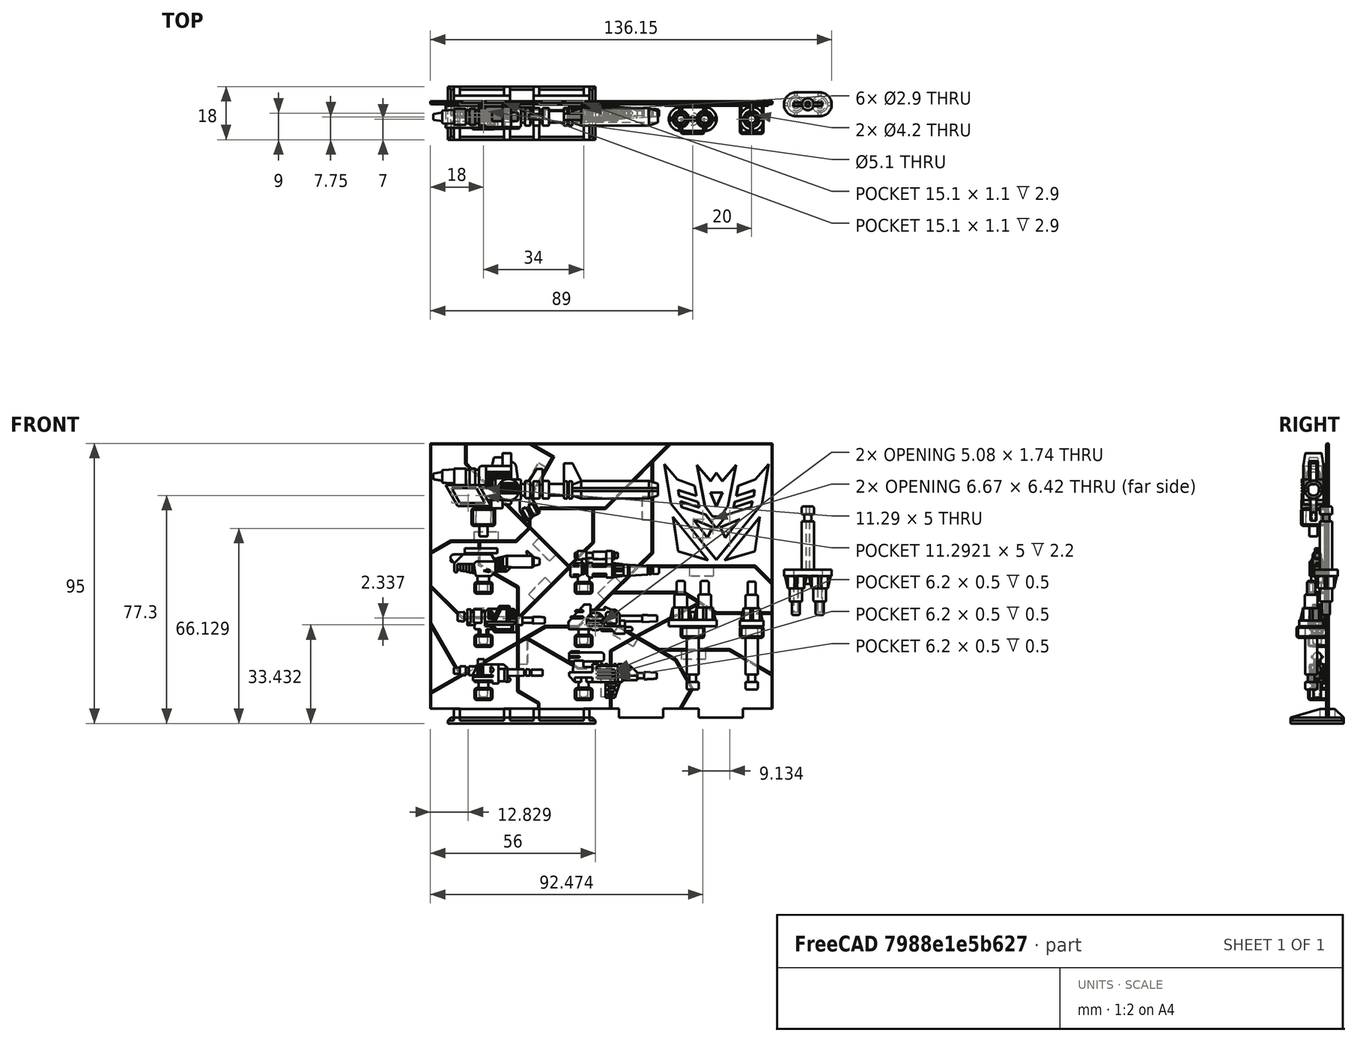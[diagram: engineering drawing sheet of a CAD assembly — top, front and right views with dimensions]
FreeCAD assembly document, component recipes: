
FREECAD ASSEMBLY — COMPONENT RECIPES ("Accesories")

This assembly document has 10 components, labeled P0..P9 below (a component is one placed body or linked part). 9 of them carry a construction recipe — the FreeCAD feature program that regenerates the part from scratch, quoted from this document or its linked companion documents; the rest are supplied as boundary geometry only. No exploded tour is included for this assembly.
NOTE — this tour is split across 3 documents so each fits a 32k-token context. This is document 1: the component sections continue in the remaining 2 documents, each repeating the header above.
COMPONENT P0 — recipe-attached ("Bonecrusher_Gun", modeled in this document).
Construction recipe (the document's own serialized feature program — sketch geometry with constraints, then the solid features built on it; lengths are millimeters unless a unit is written):

FEATURE [Sketcher::SketchObject] Sketch
  ArcFitTolerance = 1e-06
  AttachmentSupport = -> [YZ_Plane]
  FullyConstrained = true
  MakeInternals = false
  MapMode = 5
  Placement = pos=(0,0,0) rot=(0.57735,0.57735,0.57735;2.0944rad)
  sketch-geometry (1):
    g0: Circle CenterX=0 CenterY=0 CenterZ=0 NormalX=0 NormalY=0 NormalZ=1 AngleXU=0 Radius=2.25
  constraints (2):
    c: Coincident(g0,g-1)
    c: Diameter(g0) = 4.5
FEATURE [PartDesign::Pad] Pad
  Direction = (1,0,0)
  Length = 4.9
  Length2 = 10
  Placement = pos=(0,0,0) rot=(1,1,1;2.0944rad)
  Profile = -> Sketch
  ReferenceAxis = -> Sketch [N_Axis]
  Refine = true
  Suppressed = false
  Type = 0
FEATURE [Sketcher::SketchObject] Sketch001
  ArcFitTolerance = 1e-06
  AttachmentSupport = -> [Pad]
  FullyConstrained = true
  MakeInternals = false
  MapMode = 5
  Placement = pos=(4.9,0,0) rot=(0.57735,0.57735,0.57735;2.0944rad)
  sketch-geometry (1):
    g0: Circle CenterX=0 CenterY=0 CenterZ=0 NormalX=0 NormalY=0 NormalZ=1 AngleXU=0 Radius=2.45
  constraints (2):
    c: Coincident(g0,g-1)
    c: Diameter(g0) = 4.9
FEATURE [PartDesign::AdditiveLoft] AdditiveLoft
  BaseFeature = -> Pad
  Closed = false
  Placement = pos=(0,0,0) rot=(1,1,1;2.0944rad)
  Profile = -> Sketch001
  Refine = true
  Ruled = false
  Sections = -> [Pad]
  Suppressed = false
FEATURE [PartDesign::Fillet] Fillet
  Base = -> AdditiveLoft [Edge1]
  BaseFeature = -> AdditiveLoft
  Placement = pos=(0,0,0) rot=(1,1,1;2.0944rad)
  Radius = 0.5
  Refine = true
  SupportTransform = false
  Suppressed = false
  UseAllEdges = false
FEATURE [Sketcher::SketchObject] Sketch002
  ArcFitTolerance = 1e-06
  AttachmentSupport = -> [XZ_Plane]
  FullyConstrained = true
  MakeInternals = false
  MapMode = 5
  Placement = pos=(0,0,0) rot=(1,0,0;1.5708rad)
  sketch-geometry (4):
    g0: LineSegment StartX=4.2 StartY=2.5 StartZ=0 EndX=4 EndY=2.5 EndZ=0
    g1: LineSegment StartX=4 StartY=2.5 StartZ=0 EndX=4 EndY=2.3 EndZ=0
    g2: LineSegment StartX=4 StartY=2.3 StartZ=0 EndX=4.2 EndY=2.3 EndZ=0
    g3: LineSegment StartX=4.2 StartY=2.3 StartZ=0 EndX=4.2 EndY=2.5 EndZ=0
  constraints (12):
    c: Coincident(g0,g1)
    c: Coincident(g1,g2)
    c: Coincident(g2,g3)
    c: Coincident(g3,g0)
    c: Horizontal(g0)
    c: Horizontal(g2)
    c: Vertical(g1)
    c: Vertical(g3)
    c: DistanceX(g-1,g1) = 4
    c: DistanceX(g0,g0) = 0.2
    c: DistanceY(g3,g3) = 0.2
    c: DistanceY(g-1,g1) = 2.3
FEATURE [PartDesign::Groove] Groove
  Angle = 360
  Angle2 = 60
  Axis = (1,0,0)
  Base = (0,0,0)
  BaseFeature = -> Fillet
  Placement = pos=(0,0,0) rot=(1,1,1;2.0944rad)
  Profile = -> Sketch002
  ReferenceAxis = -> Sketch002 [H_Axis]
  Refine = true
  Reversed = true
  Suppressed = false
  Type = 0
FEATURE [Sketcher::SketchObject] Sketch003
  ArcFitTolerance = 1e-06
  AttachmentOffset = pos=(0,0,-1) rot=(0,0,1;0rad)
  AttachmentSupport = -> [Groove]
  FullyConstrained = true
  MakeInternals = false
  MapMode = 5
  Placement = pos=(1,0,0) rot=(0.57735,0.57735,-0.57735;4.18879rad)
  sketch-geometry (20):
    g0: LineSegment StartX=-1.5 StartY=1.5 StartZ=0 EndX=-1.32322 EndY=1.67678 EndZ=0
    g1: LineSegment StartX=-1.32322 StartY=1.67678 StartZ=0 EndX=-1.67678 EndY=2.03033 EndZ=0
    g2: LineSegment StartX=-1.67678 StartY=2.03033 StartZ=0 EndX=-2.03033 EndY=1.67678 EndZ=0
    g3: LineSegment StartX=-1.5 StartY=1.5 StartZ=0 EndX=-1.67678 EndY=1.32322 EndZ=0
    g4: LineSegment StartX=-1.67678 StartY=1.32322 StartZ=0 EndX=-2.03033 EndY=1.67678 EndZ=0
    g5: LineSegment StartX=-1.5 StartY=-1.5 StartZ=0 EndX=-1.67678 EndY=-1.32322 EndZ=0
    g6: LineSegment StartX=-1.67678 StartY=-1.32322 StartZ=0 EndX=-2.03033 EndY=-1.67678 EndZ=0
    g7: LineSegment StartX=-2.03033 StartY=-1.67678 StartZ=0 EndX=-1.67678 EndY=-2.03033 EndZ=0
    g8: LineSegment StartX=-1.67678 StartY=-2.03033 StartZ=0 EndX=-1.32322 EndY=-1.67678 EndZ=0
    g9: LineSegment StartX=-1.32322 StartY=-1.67678 StartZ=0 EndX=-1.5 EndY=-1.5 EndZ=0
    g10: LineSegment StartX=1.5 StartY=-1.5 StartZ=0 EndX=1.32322 EndY=-1.67678 EndZ=0
    g11: LineSegment StartX=1.32322 StartY=-1.67678 StartZ=0 EndX=1.67678 EndY=-2.03033 EndZ=0
    g12: LineSegment StartX=1.67678 StartY=-2.03033 StartZ=0 EndX=2.03033 EndY=-1.67678 EndZ=0
    g13: LineSegment StartX=2.03033 StartY=-1.67678 StartZ=0 EndX=1.67678 EndY=-1.32322 EndZ=0
    g14: LineSegment StartX=1.67678 StartY=-1.32322 StartZ=0 EndX=1.5 EndY=-1.5 EndZ=0
    g15: LineSegment StartX=1.5 StartY=1.5 StartZ=0 EndX=1.67678 EndY=1.32322 EndZ=0
    g16: LineSegment StartX=1.67678 StartY=1.32322 StartZ=0 EndX=2.03033 EndY=1.67678 EndZ=0
    g17: LineSegment StartX=2.03033 StartY=1.67678 StartZ=0 EndX=1.67678 EndY=2.03033 EndZ=0
    g18: LineSegment StartX=1.67678 StartY=2.03033 StartZ=0 EndX=1.32322 EndY=1.67678 EndZ=0
    g19: LineSegment StartX=1.32322 StartY=1.67678 StartZ=0 EndX=1.5 EndY=1.5 EndZ=0
  constraints (60):
    c: Coincident(g1,g0)
    c: Coincident(g2,g1)
    c: Coincident(g3,g0)
    c: Coincident(g4,g3)
    c: Coincident(g4,g2)
    c: Angle(g-1,g3) = 0.785398
    c: Angle(g0) = 0.785398
    c: Distance(g0) = 0.25
    c: Distance(g3) = 0.25
    c: Distance(g2) = 0.5
    c: Distance(g4) = 0.5
    c: Distance(g1) = 0.5
    c: Angle(g2,g1) = 1.5708
    c: DistanceY(g-1,g0) = 1.5
    c: DistanceX(g0,g-1) = 1.5
    c: Coincident(g6,g5)
    c: Coincident(g7,g6)
    c: Coincident(g8,g7)
    c: Coincident(g9,g8)
    c: Coincident(g9,g5)
    c: Coincident(g11,g10)
    c: Coincident(g12,g11)
    c: Coincident(g13,g12)
    c: Coincident(g14,g13)
    c: Coincident(g14,g10)
    c: Coincident(g16,g15)
    c: Coincident(g17,g16)
    c: Coincident(g18,g17)
    c: Coincident(g19,g18)
    c: Coincident(g19,g15)
    c: DistanceY(g-1,g15) = 1.5
    c: DistanceY(g10,g-1) = 1.5
    c: DistanceY(g5,g-1) = 1.5
    c: DistanceX(g5,g-1) = 1.5
    c: DistanceX(g-1,g15) = 1.5
    c: DistanceX(g-1,g10) = 1.5
    c: Distance(g18) = 0.5
    c: Distance(g17) = 0.5
    c: Distance(g16) = 0.5
    c: Distance(g19) = 0.25
    c: Distance(g15) = 0.25
    c: Distance(g14) = 0.25
    c: Distance(g10) = 0.25
    c: Distance(g9) = 0.25
    c: Distance(g5) = 0.25
    c: Distance(g6) = 0.5
    c: Distance(g7) = 0.5
    c: Distance(g8) = 0.5
    c: Distance(g11) = 0.5
    c: Distance(g12) = 0.5
    c: Distance(g13) = 0.5
    c: Angle(g12,g11) = 1.5708
    c: Angle(g8,g7) = 1.5708
    c: Angle(g17,g16) = 1.5708
    c: Angle(g15,g19) = 3.14159
    c: Angle(g14,g10) = 3.14159
    c: Angle(g5,g9) = 3.14159
    c: Angle(g9,g-1) = 0.785398
    c: Angle(g-1,g10) = 0.785398
    c: Angle(g-2,g19) = 0.785398
FEATURE [PartDesign::Pocket] Pocket
  BaseFeature = -> Groove
  Direction = (1,0,0)
  Length = 2
  Length2 = 5
  Placement = pos=(0,0,0) rot=(1,1,1;2.0944rad)
  Profile = -> Sketch003
  ReferenceAxis = -> Sketch003 [N_Axis]
  Refine = true
  Suppressed = false
  Type = 0
FEATURE [Sketcher::SketchObject] Sketch004
  ArcFitTolerance = 1e-06
  AttachmentSupport = -> [Pocket]
  FullyConstrained = true
  MakeInternals = false
  MapMode = 5
  Placement = pos=(4.9,0,0) rot=(0.57735,0.57735,0.57735;2.0944rad)
  sketch-geometry (1):
    g0: Circle CenterX=0 CenterY=0 CenterZ=0 NormalX=0 NormalY=0 NormalZ=1 AngleXU=0 Radius=2.1
  constraints (2):
    c: Coincident(g0,g-1)
    c: Diameter(g0) = 4.2
FEATURE [PartDesign::Pad] Pad001
  BaseFeature = -> Pocket
  Direction = (1,0,0)
  Length = 0.8
  Length2 = 10
  Placement = pos=(0,0,0) rot=(1,1,1;2.0944rad)
  Profile = -> Sketch004
  ReferenceAxis = -> Sketch004 [N_Axis]
  Refine = true
  Suppressed = false
  Type = 0
FEATURE [Sketcher::SketchObject] Sketch005
  ArcFitTolerance = 1e-06
  AttachmentSupport = -> [Pad001]
  ExternalGeometry = -> [Pad001]
  FullyConstrained = true
  MakeInternals = false
  MapMode = 5
  Placement = pos=(5.7,0,0) rot=(0.57735,0.57735,0.57735;2.0944rad)
  sketch-geometry (2):
    g0: Circle CenterX=0 CenterY=0 CenterZ=0 NormalX=0 NormalY=0 NormalZ=1 AngleXU=0 Radius=2.1
    g1: Circle CenterX=0 CenterY=0 CenterZ=0 NormalX=0 NormalY=0 NormalZ=1 AngleXU=0 Radius=2.45
  constraints (4):
    c: Coincident(g0,g-1)
    c: Diameter(g0) = 4.2
    c: Coincident(g1,g0)
    c: Radius(g1) = 2.45
FEATURE [PartDesign::Pad] Pad002
  BaseFeature = -> Pad001
  Direction = (1,0,5e-16)
  Length = 8.5
  Length2 = 10
  Placement = pos=(0,0,0) rot=(1,1,1;2.0944rad)
  Profile = -> Pad001 [Edge64]
  Refine = true
  Suppressed = false
  Type = 0
FEATURE [PartDesign::Pad] Pad003
  BaseFeature = -> Pad002
  Direction = (1,0,0)
  Length = 2
  Length2 = 10
  Placement = pos=(0,0,0) rot=(1,1,1;2.0944rad)
  Profile = -> Sketch005 [Edge2]
  ReferenceAxis = -> Sketch005 [N_Axis]
  Refine = true
  Suppressed = false
  Type = 0
FEATURE [Sketcher::SketchObject] Sketch006
  ArcFitTolerance = 1e-06
  AttachmentSupport = -> [Pad003]
  ExternalGeometry = -> [Pad003]
  FullyConstrained = true
  MakeInternals = false
  MapMode = 5
  Placement = pos=(7.7,0,0) rot=(0.57735,0.57735,0.57735;2.0944rad)
  sketch-geometry (8):
    g0: ArcOfCircle CenterX=-9.2e-15 CenterY=8.5e-15 CenterZ=0 NormalX=0 NormalY=0 NormalZ=1 AngleXU=0 Radius=2.1 StartAngle=5.78687 EndAngle=6.7795
    g1: ArcOfCircle CenterX=1.35e-14 CenterY=-3.6e-15 CenterZ=0 NormalX=0 NormalY=0 NormalZ=1 AngleXU=0 Radius=2.1 StartAngle=2.64528 EndAngle=3.63791
    g2: ArcOfCircle CenterX=-1.8e-15 CenterY=3e-16 CenterZ=0 NormalX=0 NormalY=0 NormalZ=1 AngleXU=0 Radius=2.45 StartAngle=5.77133 EndAngle=6.79504
    g3: LineSegment StartX=1.84662 StartY=-1 StartZ=0 EndX=2.136 EndY=-1.2 EndZ=0
    g4: LineSegment StartX=1.84662 StartY=1 StartZ=0 EndX=2.136 EndY=1.2 EndZ=0
    g5: ArcOfCircle CenterX=-1.5e-15 CenterY=7e-16 CenterZ=0 NormalX=0 NormalY=0 NormalZ=1 AngleXU=0 Radius=2.45 StartAngle=2.62974 EndAngle=3.65345
    g6: LineSegment StartX=-1.84662 StartY=-1 StartZ=0 EndX=-2.136 EndY=-1.2 EndZ=0
    g7: LineSegment StartX=-1.84662 StartY=1 StartZ=0 EndX=-2.136 EndY=1.2 EndZ=0
  constraints (24):
    c: Tangent(g0,g-3) = -1.5708
    c: PointOnObject(g0,g-3)
    c: Tangent(g1,g-3) = -1.5708
    c: PointOnObject(g1,g-3)
    c: Tangent(g2,g-4) = -1.5708
    c: PointOnObject(g2,g-4)
    c: Coincident(g3,g0)
    c: Coincident(g3,g2)
    c: Coincident(g4,g0)
    c: Coincident(g4,g2)
    c: DistanceY(g0,g0) = 1
    c: DistanceY(g0,g0) = 1
    c: DistanceY(g0,g2) = 1.2
    c: DistanceY(g2,g0) = 1.2
    c: Tangent(g5,g-4) = -1.5708
    c: PointOnObject(g5,g-4)
    c: DistanceY(g1,g0) = 1
    c: DistanceY(g0,g1) = 1
    c: DistanceY(g0,g5) = 1.2
    c: DistanceY(g5,g0) = 1.2
    c: Coincident(g6,g1)
    c: Coincident(g6,g5)
    c: Coincident(g7,g1)
    c: Coincident(g7,g5)
FEATURE [PartDesign::Pad] Pad004
  BaseFeature = -> Pad003
  Direction = (1,0,0)
  Length = 4.5
  Length2 = 10
  Placement = pos=(0,0,0) rot=(1,1,1;2.0944rad)
  Profile = -> Sketch006
  ReferenceAxis = -> Sketch006 [N_Axis]
  Refine = true
  Suppressed = false
  Type = 0
FEATURE [Sketcher::SketchObject] Sketch007
  ArcFitTolerance = 1e-06
  AttachmentSupport = -> [Pad004]
  FullyConstrained = true
  MakeInternals = false
  MapMode = 5
  Placement = pos=(14.2,0,7e-15) rot=(0.57735,0.57735,0.57735;2.0944rad)
  sketch-geometry (1):
    g0: Circle CenterX=0 CenterY=0 CenterZ=0 NormalX=0 NormalY=0 NormalZ=1 AngleXU=0 Radius=2.45
  constraints (2):
    c: Coincident(g0,g-1)
    c: Radius(g0) = 2.45
FEATURE [PartDesign::Pad] Pad005
  BaseFeature = -> Pad004
  Direction = (1,0,0)
  Length = 2
  Length2 = 10
  Placement = pos=(0,0,0) rot=(1,1,1;2.0944rad)
  Profile = -> Sketch007
  ReferenceAxis = -> Sketch007 [N_Axis]
  Refine = true
  Reversed = true
  Suppressed = false
  Type = 0
FEATURE [Sketcher::SketchObject] Sketch008
  ArcFitTolerance = 1e-06
  AttachmentSupport = -> [Pad005]
  FullyConstrained = true
  MakeInternals = false
  MapMode = 5
  Placement = pos=(14.2,0,0) rot=(0.57735,0.57735,0.57735;2.0944rad)
  sketch-geometry (1):
    g0: Circle CenterX=0 CenterY=0 CenterZ=0 NormalX=0 NormalY=0 NormalZ=1 AngleXU=0 Radius=1.75
  constraints (2):
    c: Coincident(g0,g-1)
    c: Diameter(g0) = 3.5
FEATURE [PartDesign::Pad] Pad006
  BaseFeature = -> Pad005
  Direction = (1,0,0)
  Length = 3.9
  Length2 = 10
  Placement = pos=(0,0,0) rot=(1,1,1;2.0944rad)
  Profile = -> Sketch008
  ReferenceAxis = -> Sketch008 [N_Axis]
  Refine = true
  Suppressed = false
  Type = 0
FEATURE [Sketcher::SketchObject] Sketch009
  ArcFitTolerance = 1e-06
  AttachmentSupport = -> [Pad006]
  FullyConstrained = true
  MakeInternals = false
  MapMode = 5
  Placement = pos=(18.1,0,0) rot=(0.57735,0.57735,0.57735;2.0944rad)
  sketch-geometry (1):
    g0: Circle CenterX=0 CenterY=0 CenterZ=0 NormalX=0 NormalY=0 NormalZ=1 AngleXU=0 Radius=1.95
  constraints (2):
    c: Coincident(g0,g-1)
    c: Diameter(g0) = 3.9
FEATURE [Sketcher::SketchObject] Sketch010
  ArcFitTolerance = 1e-06
  AttachmentOffset = pos=(0,0,12) rot=(0,0,1;0rad)
  AttachmentSupport = -> [Pad006]
  FullyConstrained = true
  MakeInternals = false
  MapMode = 5
  Placement = pos=(30.1,0,0) rot=(0.57735,0.57735,0.57735;2.0944rad)
  sketch-geometry (1):
    g0: Circle CenterX=0 CenterY=0 CenterZ=0 NormalX=0 NormalY=0 NormalZ=1 AngleXU=0 Radius=1.25
  constraints (2):
    c: Coincident(g0,g-1)
    c: Diameter(g0) = 2.5
FEATURE [PartDesign::AdditiveLoft] AdditiveLoft001
  BaseFeature = -> Pad006
  Closed = false
  Placement = pos=(0,0,0) rot=(1,1,1;2.0944rad)
  Profile = -> Sketch009
  Refine = true
  Ruled = false
  Sections = -> [Sketch010]
  Suppressed = false
FEATURE [PartDesign::Fillet] Fillet001
  Base = -> AdditiveLoft001 [Edge40]
  BaseFeature = -> AdditiveLoft001
  Placement = pos=(0,0,0) rot=(1,1,1;2.0944rad)
  Radius = 0.5
  Refine = true
  SupportTransform = false
  Suppressed = false
  UseAllEdges = false
FEATURE [Sketcher::SketchObject] Sketch011
  ArcFitTolerance = 1e-06
  AttachmentSupport = -> [XY_Plane]
  ExternalGeometry = -> [Fillet001]
  FullyConstrained = true
  MakeInternals = false
  MapMode = 5
  sketch-geometry (4):
    g0: LineSegment StartX=15 StartY=1.85 StartZ=0 EndX=15 EndY=1.65 EndZ=0
    g1: LineSegment StartX=15 StartY=1.65 StartZ=0 EndX=15.2 EndY=1.65 EndZ=0
    g2: LineSegment StartX=15.2 StartY=1.65 StartZ=0 EndX=15.2 EndY=1.85 EndZ=0
    g3: LineSegment StartX=15.2 StartY=1.85 StartZ=0 EndX=15 EndY=1.85 EndZ=0
  constraints (12):
    c: Coincident(g0,g1)
    c: Coincident(g1,g2)
    c: Coincident(g2,g3)
    c: Coincident(g3,g0)
    c: Vertical(g0)
    c: Vertical(g2)
    c: Horizontal(g1)
    c: Horizontal(g3)
    c: DistanceX(g1,g1) = 0.2
    c: DistanceY(g2,g2) = 0.2
    c: DistanceX(g-3,g0) = 0.8
    c: DistanceY(g2,g-3) = 0.6
FEATURE [PartDesign::Groove] Groove001
  Angle = 360
  Angle2 = 60
  Axis = (1,0,0)
  Base = (0,0,0)
  BaseFeature = -> Fillet001
  Placement = pos=(0,0,0) rot=(1,1,1;2.0944rad)
  Profile = -> Sketch011
  ReferenceAxis = -> Sketch011 [H_Axis]
  Refine = true
  Reversed = true
  Suppressed = false
  Type = 0
FEATURE [Sketcher::SketchObject] Sketch012
  ArcFitTolerance = 1e-06
  AttachmentSupport = -> [XZ_Plane]
  ExternalGeometry = -> [Groove001]
  FullyConstrained = true
  MakeInternals = false
  MapMode = 5
  Placement = pos=(0,0,0) rot=(1,0,0;1.5708rad)
  sketch-geometry (8):
    g0: LineSegment StartX=14.2 StartY=2.45 StartZ=0 EndX=18.1 EndY=1.95 EndZ=0
    g1: LineSegment StartX=18.1 StartY=1.95 StartZ=0 EndX=18.1 EndY=1.45 EndZ=0
    g2: LineSegment StartX=18.1 StartY=1.45 StartZ=0 EndX=14.2 EndY=1.45 EndZ=0
    g3: LineSegment StartX=14.2 StartY=2.45 StartZ=0 EndX=14.2 EndY=1.45 EndZ=0
    g4: LineSegment StartX=14.2 StartY=-2.45 StartZ=0 EndX=18.1 EndY=-1.95 EndZ=0
    g5: LineSegment StartX=18.1 StartY=-1.95 StartZ=0 EndX=18.1 EndY=-1.45 EndZ=0
    g6: LineSegment StartX=18.1 StartY=-1.45 StartZ=0 EndX=14.2 EndY=-1.45 EndZ=0
    g7: LineSegment StartX=14.2 StartY=-1.45 StartZ=0 EndX=14.2 EndY=-2.45 EndZ=0
  constraints (20):
    c: Coincident(g0,g-3)
    c: Coincident(g0,g-4)
    c: Coincident(g1,g0)
    c: PointOnObject(g1,g-4)
    c: Coincident(g2,g1)
    c: PointOnObject(g2,g-3)
    c: Horizontal(g2)
    c: Coincident(g3,g0)
    c: Coincident(g3,g2)
    c: DistanceY(g1,g1) = 0.5
    c: Coincident(g4,g-3)
    c: Coincident(g4,g-4)
    c: Coincident(g5,g4)
    c: PointOnObject(g5,g-4)
    c: Coincident(g6,g5)
    c: PointOnObject(g6,g-3)
    c: Horizontal(g6)
    c: Coincident(g7,g6)
    c: Coincident(g7,g4)
    c: DistanceY(g5,g5) = 0.5
FEATURE [PartDesign::Revolution] Revolution
  Angle = 10
  Angle2 = 60
  Axis = (1,0,0)
  Base = (0,0,0)
  BaseFeature = -> Groove001
  Placement = pos=(0,0,0) rot=(1,1,1;2.0944rad)
  Profile = -> Sketch012
  ReferenceAxis = -> Sketch012 [H_Axis]
  Refine = true
  Suppressed = false
  Type = 0
FEATURE [Sketcher::SketchObject] Sketch013
  ArcFitTolerance = 1e-06
  AttachmentSupport = -> [XY_Plane]
  ExternalGeometry = -> [Revolution]
  FullyConstrained = true
  MakeInternals = false
  MapMode = 5
  sketch-geometry (8):
    g0: LineSegment StartX=14.2 StartY=2.45 StartZ=0 EndX=18.1 EndY=1.95 EndZ=0
    g1: LineSegment StartX=18.1 StartY=1.95 StartZ=0 EndX=18.1 EndY=1.45 EndZ=0
    g2: LineSegment StartX=18.1 StartY=1.45 StartZ=0 EndX=14.2 EndY=1.45 EndZ=0
    g3: LineSegment StartX=14.2 StartY=1.45 StartZ=0 EndX=14.2 EndY=2.45 EndZ=0
    g4: LineSegment StartX=18.1 StartY=-1.95 StartZ=0 EndX=14.2 EndY=-2.45 EndZ=0
    g5: LineSegment StartX=18.1 StartY=-1.95 StartZ=0 EndX=18.1 EndY=-1.45 EndZ=0
    g6: LineSegment StartX=18.1 StartY=-1.45 StartZ=0 EndX=14.2 EndY=-1.45 EndZ=0
    g7: LineSegment StartX=14.2 StartY=-1.45 StartZ=0 EndX=14.2 EndY=-2.45 EndZ=0
  constraints (20):
    c: Coincident(g0,g-3)
    c: Coincident(g0,g-4)
    c: Coincident(g1,g0)
    c: PointOnObject(g1,g-4)
    c: Coincident(g2,g1)
    c: PointOnObject(g2,g-3)
    c: Horizontal(g2)
    c: Coincident(g3,g2)
    c: Coincident(g3,g0)
    c: DistanceY(g1,g1) = 0.5
    c: Coincident(g4,g-5)
    c: Coincident(g4,g-6)
    c: Coincident(g5,g4)
    c: PointOnObject(g5,g-5)
    c: Coincident(g6,g5)
    c: PointOnObject(g6,g-6)
    c: Horizontal(g6)
    c: Coincident(g7,g6)
    c: Coincident(g7,g4)
    c: DistanceY(g5,g5) = 0.5
FEATURE [PartDesign::Revolution] Revolution001
  Angle = 10
  Angle2 = 60
  Axis = (1,0,0)
  Base = (0,0,0)
  BaseFeature = -> Revolution
  Placement = pos=(0,0,0) rot=(1,1,1;2.0944rad)
  Profile = -> Sketch013
  ReferenceAxis = -> Sketch013 [H_Axis]
  Refine = true
  Suppressed = false
  Type = 0
FEATURE [PartDesign::Revolution] Revolution002
  Angle = 10
  Angle2 = 60
  Axis = (1,0,0)
  Base = (0,0,0)
  BaseFeature = -> Revolution001
  Placement = pos=(0,0,0) rot=(1,1,1;2.0944rad)
  Profile = -> Sketch012
  ReferenceAxis = -> Sketch012 [H_Axis]
  Refine = true
  Reversed = true
  Suppressed = false
  Type = 0
FEATURE [PartDesign::Revolution] Revolution003
  Angle = 10
  Angle2 = 60
  Axis = (1,0,0)
  Base = (0,0,0)
  BaseFeature = -> Revolution002
  Placement = pos=(0,0,0) rot=(1,1,1;2.0944rad)
  Profile = -> Sketch013
  ReferenceAxis = -> Sketch013 [H_Axis]
  Refine = true
  Reversed = true
  Suppressed = false
  Type = 0
FEATURE [Sketcher::SketchObject] Sketch014
  ArcFitTolerance = 1e-06
  AttachmentSupport = -> [Revolution003]
  ExternalGeometry = -> [Revolution003]
  FullyConstrained = false
  MakeInternals = false
  MapMode = 5
  Placement = pos=(18.1,0,0) rot=(0.57735,0.57735,-0.57735;4.18879rad)
  sketch-geometry (2):
    g0: Circle CenterX=0 CenterY=0 CenterZ=0 NormalX=0 NormalY=0 NormalZ=1 AngleXU=0 Radius=2.25
    g1: Circle CenterX=0 CenterY=0 CenterZ=0 NormalX=0 NormalY=0 NormalZ=1 AngleXU=0 Radius=1.75
  constraints (3):
    c: Coincident(g0,g-1)
    c: Diameter(g0) = 4.5
    c: Coincident(g1,g0)
FEATURE [PartDesign::Pocket] Pocket001
  BaseFeature = -> Revolution003
  Direction = (1,-1.3e-15,0)
  Length = 0.4
  Length2 = 5
  Placement = pos=(0,0,0) rot=(1,1,1;2.0944rad)
  Profile = -> Sketch014
  ReferenceAxis = -> Sketch014 [N_Axis]
  Refine = true
  Reversed = true
  Suppressed = false
  Type = 0
FEATURE [Sketcher::SketchObject] Sketch015
  ArcFitTolerance = 1e-06
  AttachmentSupport = -> [XZ_Plane]
  ExternalGeometry = -> [Pocket001]
  FullyConstrained = true
  MakeInternals = false
  MapMode = 5
  Placement = pos=(0,0,0) rot=(1,0,0;1.5708rad)
  sketch-geometry (12):
    g0: LineSegment StartX=19.6 StartY=2.12038 StartZ=0 EndX=19.6 EndY=1.62038 EndZ=0
    g1: LineSegment StartX=19.6 StartY=1.62038 StartZ=0 EndX=20.1 EndY=1.62038 EndZ=0
    g2: LineSegment StartX=20.1 StartY=1.62038 StartZ=0 EndX=20.1 EndY=2.12038 EndZ=0
    g3: LineSegment StartX=20.1 StartY=2.12038 StartZ=0 EndX=19.6 EndY=2.12038 EndZ=0
    g4: LineSegment StartX=26.3291 StartY=1.67747 StartZ=0 EndX=26.3291 EndY=1.17747 EndZ=0
    g5: LineSegment StartX=26.3291 StartY=1.17747 StartZ=0 EndX=26.8291 EndY=1.17747 EndZ=0
    g6: LineSegment StartX=26.8291 StartY=1.17747 StartZ=0 EndX=26.8291 EndY=1.67747 EndZ=0
    g7: LineSegment StartX=26.8291 StartY=1.67747 StartZ=0 EndX=26.3291 EndY=1.67747 EndZ=0
    g8: LineSegment StartX=27.6291 StartY=1.57747 StartZ=0 EndX=27.6291 EndY=1.07747 EndZ=0
    g9: LineSegment StartX=27.6291 StartY=1.07747 StartZ=0 EndX=28.1291 EndY=1.07747 EndZ=0
    g10: LineSegment StartX=28.1291 StartY=1.07747 StartZ=0 EndX=28.1291 EndY=1.57747 EndZ=0
    g11: LineSegment StartX=28.1291 StartY=1.57747 StartZ=0 EndX=27.6291 EndY=1.57747 EndZ=0
  constraints (36):
    c: Coincident(g0,g1)
    c: Coincident(g1,g2)
    c: Coincident(g2,g3)
    c: Coincident(g3,g0)
    c: Vertical(g0)
    c: Vertical(g2)
    c: Horizontal(g1)
    c: Horizontal(g3)
    c: Coincident(g4,g5)
    c: Coincident(g5,g6)
    c: Coincident(g6,g7)
    c: Coincident(g7,g4)
    c: Vertical(g4)
    c: Vertical(g6)
    c: Horizontal(g5)
    c: Horizontal(g7)
    c: Coincident(g8,g9)
    c: Coincident(g9,g10)
    c: Coincident(g10,g11)
    c: Coincident(g11,g8)
    c: Vertical(g8)
    c: Vertical(g10)
    c: Horizontal(g9)
    c: Horizontal(g11)
    c: DistanceX(g7,g7) = 0.5
    c: DistanceX(g11,g11) = 0.5
    c: DistanceX(g3,g3) = 0.5
    c: DistanceY(g2,g2) = 0.5
    c: DistanceY(g6,g6) = 0.5
    c: DistanceY(g10,g10) = 0.5
    c: DistanceX(g-3,g0) = 1.5
    c: DistanceX(g9,g-4) = 1.5
    c: DistanceX(g5,g8) = 0.8
    c: DistanceY(g9,g-4) = 0.2
    c: DistanceY(g8,g5) = 0.1
    c: DistanceY(g0,g-3) = 0.3
FEATURE [PartDesign::Groove] Groove002
  Angle = 360
  Angle2 = 60
  Axis = (1,0,0)
  Base = (0,0,0)
  BaseFeature = -> Pocket001
  Placement = pos=(0,0,0) rot=(1,1,1;2.0944rad)
  Profile = -> Sketch015
  ReferenceAxis = -> Sketch015 [H_Axis]
  Refine = true
  Reversed = true
  Suppressed = false
  Type = 0
FEATURE [Sketcher::SketchObject] Sketch016
  ArcFitTolerance = 1e-06
  AttachmentSupport = -> [XY_Plane]
  ExternalGeometry = -> [Groove002]
  FullyConstrained = false
  MakeInternals = false
  MapMode = 5
  sketch-geometry (5):
    g0: LineSegment StartX=4 StartY=0 StartZ=0 EndX=4 EndY=0.8 EndZ=0
    g1: LineSegment StartX=4 StartY=0.8 StartZ=0 EndX=5.5 EndY=0.8 EndZ=0
    g2: LineSegment StartX=5.5 StartY=0.8 StartZ=0 EndX=5.5 EndY=-0.8 EndZ=0
    g3: LineSegment StartX=5.5 StartY=-0.8 StartZ=0 EndX=4 EndY=-0.8 EndZ=0
    g4: LineSegment StartX=4 StartY=-0.8 StartZ=0 EndX=4 EndY=0 EndZ=0
  constraints (13):
    c: PointOnObject(g0,g-3)
    c: Coincident(g1,g0)
    c: Horizontal(g1)
    c: Coincident(g2,g1)
    c: Vertical(g2)
    c: Coincident(g3,g2)
    c: PointOnObject(g3,g-3)
    c: Horizontal(g3)
    c: Coincident(g4,g3)
    c: Coincident(g4,g0)
    c: DistanceY(g0,g0) = 0.8
    c: DistanceY(g4,g4) = 0.8
    c: DistanceX(g1,g1) = 1.5
FEATURE [PartDesign::Pad] Pad007
  BaseFeature = -> Groove002
  Direction = (0,0,1)
  Length = 5
  Length2 = 10
  Placement = pos=(0,0,0) rot=(1,1,1;2.0944rad)
  Profile = -> Sketch016
  ReferenceAxis = -> Sketch016 [N_Axis]
  Refine = true
  Suppressed = false
  Type = 0
FEATURE [Sketcher::SketchObject] Sketch017
  ArcFitTolerance = 1e-06
  AttachmentSupport = -> [Pad007]
  ExternalGeometry = -> [Pad007]
  FullyConstrained = true
  MakeInternals = false
  MapMode = 5
  Placement = pos=(4,0,0) rot=(0.57735,0.57735,-0.57735;4.18879rad)
  sketch-geometry (1):
    g0: Circle CenterX=0 CenterY=-5 CenterZ=0 NormalX=0 NormalY=0 NormalZ=1 AngleXU=0 Radius=1.45
  constraints (2):
    c: Symmetric(g-3,g-3,g0)
    c: Diameter(g0) = 2.9
FEATURE [PartDesign::Pad] Pad008
  BaseFeature = -> Pad007
  Direction = (-1,0,0)
  Length = 1.5
  Length2 = 10
  Placement = pos=(0,0,0) rot=(1,1,1;2.0944rad)
  Profile = -> Sketch017 [Edge1]
  ReferenceAxis = -> Sketch017 [N_Axis]
  Refine = true
  Suppressed = false
  Type = 0
FEATURE [PartDesign::Pad] Pad009
  BaseFeature = -> Pad008
  Direction = (-1,0,0)
  Length = 1.5
  Length2 = 10
  Placement = pos=(0,0,0) rot=(1,1,1;2.0944rad)
  Profile = -> Sketch017
  ReferenceAxis = -> Sketch017 [N_Axis]
  Refine = true
  Reversed = true
  Suppressed = false
  Type = 0
FEATURE [Sketcher::SketchObject] Sketch018
  ArcFitTolerance = 1e-06
  AttachmentSupport = -> [Pad009]
  ExternalGeometry = -> [Pad009]
  FullyConstrained = true
  MakeInternals = false
  MapMode = 5
  Placement = pos=(2.5,0,0) rot=(0.57735,0.57735,-0.57735;4.18879rad)
  sketch-geometry (1):
    g0: Circle CenterX=0 CenterY=-5 CenterZ=0 NormalX=0 NormalY=0 NormalZ=1 AngleXU=0 Radius=0.9
  constraints (2):
    c: Coincident(g0,g-3)
    c: Diameter(g0) = 1.8
FEATURE [PartDesign::Body] Body  label="Bonecrusher_Gun"
  AllowCompound = false
  Group = -> [Sketch,Pad,Sketch001,AdditiveLoft,Fillet,Sketch002,Groove,Sketch003,Pocket,Sketch004,Pad001,Sketch005,Pad002,Pad003,Sketch006,Pad004,Sketch007,Pad005,Sketch008,Pad006,Sketch009,Sketch010,AdditiveLoft001,Fillet001,Sketch011,Groove001,Sketch012,Revolution,Sketch013,Revolution001,Revolution002,Revolution003,Sketch014,Pocket001,Sketch015,Groove002,Sketch016,Pad007,Sketch017,Pad008,Pad009,Sketch018,+17 more]
  Origin = -> Origin
  Placement = pos=(-10.55,-3,2) rot=(0,0,1;0rad)
  Tip = -> Fillet003
COMPONENT P1 — recipe-attached ("Devastator_Gun", modeled in this document).
Construction recipe (the document's own serialized feature program — sketch geometry with constraints, then the solid features built on it; lengths are millimeters unless a unit is written):

FEATURE [Sketcher::SketchObject] Sketch171
  ArcFitTolerance = 1e-06
  AttachmentSupport = -> [XY_Plane020]
  FullyConstrained = true
  MakeInternals = false
  MapMode = 5
  sketch-geometry (4):
    g0: LineSegment StartX=-4.04145 StartY=7 StartZ=0 EndX=0 EndY=0 EndZ=0
    g1: LineSegment StartX=0 StartY=0 StartZ=0 EndX=11.3 EndY=0 EndZ=0
    g2: LineSegment StartX=11.3 StartY=0 StartZ=0 EndX=7.25855 EndY=7 EndZ=0
    g3: LineSegment StartX=7.25855 StartY=7 StartZ=0 EndX=-4.04145 EndY=7 EndZ=0
  constraints (11):
    c: Coincident(g1,g0)
    c: PointOnObject(g1,g-1)
    c: DistanceX(g1,g1) = 11.3
    c: Coincident(g0,g-1)
    c: Coincident(g2,g1)
    c: Coincident(g3,g2)
    c: Coincident(g3,g0)
    c: Horizontal(g3)
    c: Parallel(g0,g2)
    c: DistanceY(g0,g0) = 7
    c: Angle(g0,g3) = 1.0472
FEATURE [PartDesign::Pad] Pad134
  Direction = (0,0,1)
  Length = 7.5
  Length2 = 10
  Profile = -> Sketch171
  ReferenceAxis = -> Sketch171 [N_Axis]
  Refine = true
  Suppressed = false
  Type = 0
FEATURE [Sketcher::SketchObject] Sketch172
  ArcFitTolerance = 1e-06
  AttachmentSupport = -> [Pad134]
  ExternalGeometry = -> [Pad134]
  FullyConstrained = true
  MakeInternals = false
  MapMode = 5
  Placement = pos=(0,0,7.5) rot=(0,0,1;0rad)
  sketch-geometry (4):
    g0: LineSegment StartX=-2.01675 StartY=6 StartZ=0 EndX=6.38855 EndY=6 EndZ=0
    g1: LineSegment StartX=6.38855 StartY=6 StartZ=0 EndX=9.2753 EndY=1 EndZ=0
    g2: LineSegment StartX=9.2753 StartY=1 StartZ=0 EndX=0.87 EndY=1 EndZ=0
    g3: LineSegment StartX=0.87 StartY=1 StartZ=0 EndX=-2.01675 EndY=6 EndZ=0
  constraints (14):
    c: Horizontal(g0)
    c: Coincident(g1,g0)
    c: Coincident(g2,g1)
    c: Horizontal(g2)
    c: Coincident(g3,g2)
    c: Coincident(g3,g0)
    c: DistanceY(g0,g-6) = 1
    c: DistanceY(g-5,g1) = 1
    c: Parallel(g3,g-6)
    c: Parallel(g1,g-4)
    c: DistanceY(g2,g0) = 5
    c: DistanceX(g0,g-4) = 0.87
    c: DistanceX(g-1,g2) = 0.87
    c: DistanceX(g2,g1) = 8.4053
FEATURE [PartDesign::Pocket] Pocket002
  BaseFeature = -> Pad134
  Direction = (0,0,-1)
  Length = 2.2
  Length2 = 5
  Profile = -> Sketch172
  ReferenceAxis = -> Sketch172 [N_Axis]
  Refine = true
  Suppressed = false
  Type = 0
FEATURE [Sketcher::SketchObject] Sketch173
  ArcFitTolerance = 1e-06
  AttachmentSupport = -> [Pocket002]
  ExternalGeometry = -> [Pocket002]
  FullyConstrained = true
  MakeInternals = false
  MapMode = 5
  Placement = pos=(0,0,0) rot=(1,0,0;3.14159rad)
  sketch-geometry (4):
    g0: LineSegment StartX=0.87 StartY=-1 StartZ=0 EndX=9.2753 EndY=-1 EndZ=0
    g1: LineSegment StartX=9.2753 StartY=-1 StartZ=0 EndX=6.38855 EndY=-6 EndZ=0
    g2: LineSegment StartX=6.38855 StartY=-6 StartZ=0 EndX=-2.01675 EndY=-6 EndZ=0
    g3: LineSegment StartX=-2.01675 StartY=-6 StartZ=0 EndX=0.87 EndY=-1 EndZ=0
  constraints (12):
    c: Horizontal(g0)
    c: Coincident(g1,g0)
    c: Coincident(g2,g1)
    c: Horizontal(g2)
    c: Coincident(g3,g2)
    c: Coincident(g3,g0)
    c: Parallel(g3,g-6)
    c: Parallel(g1,g-4)
    c: DistanceY(g-5,g1) = 1
    c: DistanceY(g0,g-1) = 1
    c: DistanceX(g-1,g0) = 0.87
    c: DistanceX(g1,g-5) = 0.87
FEATURE [PartDesign::Pocket] Pocket003
  BaseFeature = -> Pocket002
  Direction = (0,0,1)
  Length = 2.2
  Length2 = 5
  Profile = -> Sketch173
  ReferenceAxis = -> Sketch173 [N_Axis]
  Refine = true
  Suppressed = false
  Type = 0
FEATURE [Sketcher::SketchObject] Sketch174
  ArcFitTolerance = 1e-06
  AttachmentSupport = -> [Pocket003]
  ExternalGeometry = -> [Pocket003]
  FullyConstrained = true
  MakeInternals = false
  MapMode = 5
  Placement = pos=(0,0,7.5) rot=(0,0,1;0rad)
  sketch-geometry (15):
    g0: LineSegment StartX=11.0113 StartY=0.5 StartZ=0 EndX=18.0113 EndY=0.5 EndZ=0
    g1: LineSegment StartX=18.0113 StartY=0.5 StartZ=0 EndX=18.4585 EndY=2 EndZ=0
    g2: LineSegment StartX=18.4585 StartY=2 StartZ=0 EndX=21.4585 EndY=2 EndZ=0
    g3: LineSegment StartX=21.4585 StartY=2 StartZ=0 EndX=21.4585 EndY=9 EndZ=0
    g4: LineSegment StartX=21.4585 StartY=9 StartZ=0 EndX=20.4585 EndY=9 EndZ=0
    g5: LineSegment StartX=20.4585 StartY=9 StartZ=0 EndX=19.7585 EndY=14 EndZ=0
    g6: LineSegment StartX=19.7585 StartY=14 StartZ=0 EndX=18.2585 EndY=15.2 EndZ=0
    g7: LineSegment StartX=18.2585 StartY=15.2 StartZ=0 EndX=18.2585 EndY=17.9 EndZ=0
    g8: LineSegment StartX=18.2585 StartY=17.9 StartZ=0 EndX=15.2585 EndY=17.9 EndZ=0
    g9: LineSegment StartX=15.2585 StartY=17.9 StartZ=0 EndX=15.2585 EndY=16.4 EndZ=0
    g10: LineSegment StartX=15.2585 StartY=16.4 StartZ=0 EndX=12.2585 EndY=16.4 EndZ=0
    g11: LineSegment StartX=12.2585 StartY=16.4 StartZ=0 EndX=11.7585 EndY=13.5 EndZ=0
    g12: LineSegment StartX=11.7585 StartY=13.5 StartZ=0 EndX=7.25855 EndY=13.5 EndZ=0
    g13: LineSegment StartX=7.25855 StartY=13.5 StartZ=0 EndX=7.25855 EndY=7 EndZ=0
    g14: LineSegment StartX=11.0113 StartY=0.5 StartZ=0 EndX=7.25855 EndY=7 EndZ=0
  constraints (46):
    c: PointOnObject(g0,g-3)
    c: Horizontal(g0)
    c: Coincident(g1,g0)
    c: Coincident(g2,g1)
    c: Horizontal(g2)
    c: Coincident(g3,g2)
    c: Vertical(g3)
    c: Coincident(g4,g3)
    c: Horizontal(g4)
    c: Coincident(g5,g4)
    c: Coincident(g6,g5)
    c: Coincident(g7,g6)
    c: Vertical(g7)
    c: Coincident(g8,g7)
    c: Horizontal(g8)
    c: Coincident(g9,g8)
    c: Vertical(g9)
    c: Coincident(g10,g9)
    c: Horizontal(g10)
    c: Coincident(g11,g10)
    c: Coincident(g12,g11)
    c: Horizontal(g12)
    c: Coincident(g13,g12)
    c: Coincident(g13,g-3)
    c: Vertical(g13)
    c: DistanceX(g0,g0) = 7
    c: DistanceY(g13,g13) = 6.5
    c: DistanceX(g12,g12) = 4.5
    c: DistanceY(g11,g10) = 2.9
    c: DistanceY(g9,g9) = 1.5
    c: DistanceY(g-3,g0) = 0.5
    c: DistanceX(g8,g8) = 3
    c: DistanceY(g3,g3) = 7
    c: DistanceX(g6,g5) = 1.5
    c: DistanceX(g-4,g3) = 25.5
    c: DistanceX(g2,g2) = 3
    c: DistanceX(g-1,g2) = 21.4585
    c: DistanceY(g7,g7) = 2.7
    c: DistanceY(g0,g1) = 1.5
    c: DistanceX(g10,g10) = 3
    c: DistanceX(g12,g3) = 14.2
    c: Coincident(g14,g0)
    c: Coincident(g14,g13)
    c: DistanceY(g4,g5) = 5
    c: DistanceX(g4,g3) = 1
    c: DistanceX(g5,g4) = 0.7
FEATURE [PartDesign::Pad] Pad135
  BaseFeature = -> Pocket003
  Direction = (0,0,1)
  Length = 7.5
  Length2 = 10
  Profile = -> Sketch174
  ReferenceAxis = -> Sketch174 [N_Axis]
  Refine = true
  Reversed = true
  Suppressed = false
  Type = 0
FEATURE [Sketcher::SketchObject] Sketch175
  ArcFitTolerance = 1e-06
  AttachmentSupport = -> [Pad135]
  ExternalGeometry = -> [Pad135]
  FullyConstrained = true
  MakeInternals = false
  MapMode = 5
  Placement = pos=(0,0,7.5) rot=(0,0,1;0rad)
  sketch-geometry (15):
    g0: LineSegment StartX=7.25855 StartY=7 StartZ=0 EndX=11.0113 EndY=0.5 EndZ=0
    g1: LineSegment StartX=7.25855 StartY=7 StartZ=0 EndX=7.25855 EndY=13.5 EndZ=0
    g2: LineSegment StartX=7.25855 StartY=13.5 StartZ=0 EndX=11.7585 EndY=13.5 EndZ=0
    g3: LineSegment StartX=11.7585 StartY=13.5 StartZ=0 EndX=12.2585 EndY=16.4 EndZ=0
    g4: LineSegment StartX=12.2585 StartY=16.4 StartZ=0 EndX=15.2585 EndY=16.4 EndZ=0
    g5: LineSegment StartX=15.2585 StartY=16.4 StartZ=0 EndX=15.2585 EndY=17.9 EndZ=0
    g6: LineSegment StartX=15.2585 StartY=17.9 StartZ=0 EndX=18.2585 EndY=17.9 EndZ=0
    g7: LineSegment StartX=18.2585 StartY=17.9 StartZ=0 EndX=18.2585 EndY=15.2 EndZ=0
    g8: LineSegment StartX=18.2585 StartY=15.2 StartZ=0 EndX=19.7585 EndY=14 EndZ=0
    g9: LineSegment StartX=19.7585 StartY=14 StartZ=0 EndX=20.4585 EndY=9 EndZ=0
    g10: LineSegment StartX=20.4585 StartY=9 StartZ=0 EndX=21.4585 EndY=9 EndZ=0
    g11: LineSegment StartX=21.4585 StartY=9 StartZ=0 EndX=21.4585 EndY=2 EndZ=0
    g12: LineSegment StartX=21.4585 StartY=2 StartZ=0 EndX=18.4585 EndY=2 EndZ=0
    g13: LineSegment StartX=18.4585 StartY=2 StartZ=0 EndX=18.0113 EndY=0.5 EndZ=0
    g14: LineSegment StartX=18.0113 StartY=0.5 StartZ=0 EndX=11.0113 EndY=0.5 EndZ=0
  constraints (30):
    c: Coincident(g0,g-3)
    c: Coincident(g0,g-16)
    c: Coincident(g1,g0)
    c: Coincident(g1,g-4)
    c: Coincident(g2,g1)
    c: Coincident(g2,g-5)
    c: Coincident(g3,g2)
    c: Coincident(g3,g-6)
    c: Coincident(g4,g3)
    c: Coincident(g4,g-6)
    c: Coincident(g5,g4)
    c: Coincident(g5,g-8)
    c: Coincident(g6,g5)
    c: Coincident(g6,g-9)
    c: Coincident(g7,g6)
    c: Coincident(g7,g-10)
    c: Coincident(g8,g7)
    c: Coincident(g8,g-11)
    c: Coincident(g9,g8)
    c: Coincident(g9,g-12)
    c: Coincident(g10,g9)
    c: Coincident(g10,g-13)
    c: Coincident(g11,g10)
    c: Coincident(g11,g-14)
    c: Coincident(g12,g11)
    c: Coincident(g12,g-15)
    c: Coincident(g13,g12)
    c: Coincident(g13,g-16)
    c: Coincident(g14,g13)
    c: Coincident(g14,g0)
FEATURE [PartDesign::Pocket] Pocket004
  BaseFeature = -> Pad135
  Direction = (0,0,-1)
  Length = 0.3
  Length2 = 5
  Profile = -> Sketch175
  ReferenceAxis = -> Sketch175 [N_Axis]
  Refine = true
  Suppressed = false
  Type = 0
FEATURE [Sketcher::SketchObject] Sketch176
  ArcFitTolerance = 1e-06
  AttachmentSupport = -> [Pocket004]
  ExternalGeometry = -> [Pocket004]
  FullyConstrained = true
  MakeInternals = false
  MapMode = 5
  Placement = pos=(0,0,0) rot=(1,0,0;3.14159rad)
  sketch-geometry (15):
    g0: LineSegment StartX=7.25855 StartY=-7 StartZ=0 EndX=11.0113 EndY=-0.5 EndZ=0
    g1: LineSegment StartX=11.0113 StartY=-0.5 StartZ=0 EndX=18.0113 EndY=-0.5 EndZ=0
    g2: LineSegment StartX=18.0113 StartY=-0.5 StartZ=0 EndX=18.4585 EndY=-2 EndZ=0
    g3: LineSegment StartX=18.4585 StartY=-2 StartZ=0 EndX=21.4585 EndY=-2 EndZ=0
    g4: LineSegment StartX=21.4585 StartY=-2 StartZ=0 EndX=21.4585 EndY=-9 EndZ=0
    g5: LineSegment StartX=21.4585 StartY=-9 StartZ=0 EndX=20.4585 EndY=-9 EndZ=0
    g6: LineSegment StartX=20.4585 StartY=-9 StartZ=0 EndX=19.7585 EndY=-14 EndZ=0
    g7: LineSegment StartX=19.7585 StartY=-14 StartZ=0 EndX=18.2585 EndY=-15.2 EndZ=0
    g8: LineSegment StartX=18.2585 StartY=-15.2 StartZ=0 EndX=18.2585 EndY=-17.9 EndZ=0
    g9: LineSegment StartX=18.2585 StartY=-17.9 StartZ=0 EndX=15.2585 EndY=-17.9 EndZ=0
    g10: LineSegment StartX=15.2585 StartY=-17.9 StartZ=0 EndX=15.2585 EndY=-16.4 EndZ=0
    g11: LineSegment StartX=15.2585 StartY=-16.4 StartZ=0 EndX=12.2585 EndY=-16.4 EndZ=0
    g12: LineSegment StartX=12.2585 StartY=-16.4 StartZ=0 EndX=11.7585 EndY=-13.5 EndZ=0
    g13: LineSegment StartX=11.7585 StartY=-13.5 StartZ=0 EndX=7.25855 EndY=-13.5 EndZ=0
    g14: LineSegment StartX=7.25855 StartY=-13.5 StartZ=0 EndX=7.25855 EndY=-7 EndZ=0
  constraints (30):
    c: Coincident(g0,g-16)
    c: Coincident(g0,g-3)
    c: Coincident(g1,g0)
    c: Coincident(g1,g-4)
    c: Coincident(g2,g1)
    c: Coincident(g2,g-5)
    c: Coincident(g3,g2)
    c: Coincident(g3,g-6)
    c: Coincident(g4,g3)
    c: Coincident(g4,g-7)
    c: Coincident(g5,g4)
    c: Coincident(g5,g-8)
    c: Coincident(g6,g5)
    c: Coincident(g6,g-9)
    c: Coincident(g7,g6)
    c: Coincident(g7,g-10)
    c: Coincident(g8,g7)
    c: Coincident(g8,g-11)
    c: Coincident(g9,g8)
    c: Coincident(g9,g-12)
    c: Coincident(g10,g9)
    c: Coincident(g10,g-13)
    c: Coincident(g11,g10)
    c: Coincident(g11,g-14)
    c: Coincident(g12,g11)
    c: Coincident(g12,g-15)
    c: Coincident(g13,g12)
    c: Coincident(g13,g-16)
    c: Coincident(g14,g13)
    c: Coincident(g14,g0)
FEATURE [PartDesign::Pocket] Pocket005
  BaseFeature = -> Pocket004
  Direction = (0,0,1)
  Length = 0.3
  Length2 = 5
  Profile = -> Sketch176
  ReferenceAxis = -> Sketch176 [N_Axis]
  Refine = true
  Suppressed = false
  Type = 0
FEATURE [Sketcher::SketchObject] Sketch177
  ArcFitTolerance = 1e-06
  AttachmentSupport = -> [Pocket005]
  ExternalGeometry = -> [Pocket005]
  FullyConstrained = true
  MakeInternals = false
  MapMode = 5
  Placement = pos=(0,0,7.2) rot=(0,0,1;0rad)
  sketch-geometry (3):
    g0: Circle CenterX=17.3282 CenterY=5.47056 CenterZ=0 NormalX=0 NormalY=0 NormalZ=1 AngleXU=0 Radius=3.65
    g1: LineSegment [constr] StartX=18.2585 StartY=15.2 StartZ=0 EndX=18.2585 EndY=9 EndZ=0
    g2: LineSegment [constr] StartX=20.4585 StartY=9 StartZ=0 EndX=18.2585 EndY=9 EndZ=0
  constraints (8):
    c: PointOnObject(g-4,g0)
    c: Coincident(g1,g-5)
    c: PointOnObject(g1,g0)
    c: Vertical(g1)
    c: Coincident(g2,g-3)
    c: Coincident(g2,g1)
    c: Horizontal(g2)
    c: Diameter(g0) = 7.3
FEATURE [PartDesign::Pad] Pad136
  BaseFeature = -> Pocket005
  Direction = (0,0,1)
  Length = 0.55
  Length2 = 10
  Profile = -> Sketch177
  ReferenceAxis = -> Sketch177 [N_Axis]
  Refine = true
  Suppressed = false
  Type = 0
FEATURE [Sketcher::SketchObject] Sketch178
  ArcFitTolerance = 1e-06
  AttachmentSupport = -> [Pad136]
  ExternalGeometry = -> [Pad136]
  FullyConstrained = true
  MakeInternals = false
  MapMode = 5
  Placement = pos=(0,0,0.3) rot=(1,0,0;3.14159rad)
  sketch-geometry (3):
    g0: Circle CenterX=17.3282 CenterY=-5.47056 CenterZ=0 NormalX=0 NormalY=0 NormalZ=1 AngleXU=0 Radius=3.65
    g1: LineSegment [constr] StartX=18.2585 StartY=-15.2 StartZ=0 EndX=18.2585 EndY=-9 EndZ=0
    g2: LineSegment [constr] StartX=20.4585 StartY=-9 StartZ=0 EndX=18.2585 EndY=-9 EndZ=0
  constraints (8):
    c: Diameter(g0) = 7.3
    c: PointOnObject(g-3,g0)
    c: Coincident(g1,g-6)
    c: PointOnObject(g1,g0)
    c: Vertical(g1)
    c: Coincident(g2,g-5)
    c: Coincident(g2,g1)
    c: Horizontal(g2)
FEATURE [PartDesign::Pad] Pad137
  BaseFeature = -> Pad136
  Direction = (0,0,-1)
  Length = 0.55
  Length2 = 10
  Profile = -> Sketch178
  ReferenceAxis = -> Sketch178 [N_Axis]
  Refine = true
  Suppressed = false
  Type = 0
FEATURE [Sketcher::SketchObject] Sketch179
  ArcFitTolerance = 1e-06
  AttachmentSupport = -> [Pad137]
  ExternalGeometry = -> [Pad137]
  FullyConstrained = true
  MakeInternals = false
  MapMode = 5
  Placement = pos=(0,0,7.2) rot=(0,0,1;0rad)
FEATURE [Sketcher::SketchObject] Sketch180
  ArcFitTolerance = 1e-06
  AttachmentSupport = -> [Pad137]
  ExternalGeometry = -> [Pad137]
  FullyConstrained = true
  MakeInternals = false
  MapMode = 5
  Placement = pos=(0,0,7.2) rot=(0,0,1;0rad)
  sketch-geometry (4):
    g0: LineSegment StartX=18.2585 StartY=15.2 StartZ=0 EndX=19.7585 EndY=14 EndZ=0
    g1: LineSegment StartX=19.7585 StartY=14 StartZ=0 EndX=20.4585 EndY=9 EndZ=0
    g2: LineSegment StartX=18.2585 StartY=15.2 StartZ=0 EndX=18.2585 EndY=9 EndZ=0
    g3: LineSegment StartX=20.4585 StartY=9 StartZ=0 EndX=18.2585 EndY=9 EndZ=0
  constraints (9):
    c: Coincident(g0,g-3)
    c: Coincident(g0,g-4)
    c: Coincident(g1,g0)
    c: Coincident(g1,g-4)
    c: Coincident(g2,g0)
    c: PointOnObject(g2,g-5)
    c: Vertical(g2)
    c: Coincident(g3,g1)
    c: Coincident(g3,g2)
FEATURE [PartDesign::Pocket] Pocket006
  BaseFeature = -> Pad137
  Direction = (0,0,-1)
  Length = 1.95
  Length2 = 5
  Profile = -> Sketch180
  ReferenceAxis = -> Sketch180 [N_Axis]
  Refine = true
  Suppressed = false
  Type = 0
FEATURE [Sketcher::SketchObject] Sketch181
  ArcFitTolerance = 1e-06
  AttachmentSupport = -> [Pocket006]
  ExternalGeometry = -> [Pocket006]
  FullyConstrained = true
  MakeInternals = false
  MapMode = 5
  Placement = pos=(0,0,0.3) rot=(1,0,0;3.14159rad)
  sketch-geometry (4):
    g0: LineSegment StartX=18.2585 StartY=-15.2 StartZ=0 EndX=19.7585 EndY=-14 EndZ=0
    g1: LineSegment StartX=19.7585 StartY=-14 StartZ=0 EndX=20.4585 EndY=-9 EndZ=0
    g2: LineSegment StartX=20.4585 StartY=-9 StartZ=0 EndX=18.2585 EndY=-9 EndZ=0
    g3: LineSegment StartX=18.2585 StartY=-15.2 StartZ=0 EndX=18.2585 EndY=-9 EndZ=0
  constraints (9):
    c: Coincident(g0,g-4)
    c: Coincident(g0,g-4)
    c: Coincident(g1,g0)
    c: Coincident(g1,g-3)
    c: Coincident(g2,g1)
    c: PointOnObject(g2,g-5)
    c: Horizontal(g2)
    c: Coincident(g3,g0)
    c: Coincident(g3,g2)
FEATURE [PartDesign::Pocket] Pocket007
  BaseFeature = -> Pocket006
  Direction = (0,0,1)
  Length = 1.95
  Length2 = 5
  Profile = -> Sketch181
  ReferenceAxis = -> Sketch181 [N_Axis]
  Refine = true
  Suppressed = false
  Type = 0
FEATURE [Sketcher::SketchObject] Sketch182
  ArcFitTolerance = 1e-06
  AttachmentSupport = -> [Pocket007]
  ExternalGeometry = -> [Pocket007]
  FullyConstrained = true
  MakeInternals = false
  MapMode = 5
  Placement = pos=(0,0,0.3) rot=(1,0,0;3.14159rad)
  sketch-geometry (4):
    g0: LineSegment StartX=15.2585 StartY=-16.4 StartZ=0 EndX=15.2585 EndY=-13.5 EndZ=0
    g1: LineSegment StartX=11.7585 StartY=-13.5 StartZ=0 EndX=15.2585 EndY=-13.5 EndZ=0
    g2: LineSegment StartX=15.2585 StartY=-16.4 StartZ=0 EndX=12.2585 EndY=-16.4 EndZ=0
    g3: LineSegment StartX=12.2585 StartY=-16.4 StartZ=0 EndX=11.7585 EndY=-13.5 EndZ=0
  constraints (9):
    c: Coincident(g0,g-3)
    c: Vertical(g0)
    c: Coincident(g1,g-4)
    c: Coincident(g1,g0)
    c: Horizontal(g1)
    c: Coincident(g2,g0)
    c: Coincident(g2,g-4)
    c: Coincident(g3,g2)
    c: Coincident(g3,g1)
FEATURE [PartDesign::Pocket] Pocket008
  BaseFeature = -> Pocket007
  Direction = (0,0,1)
  Length = 1.95
  Length2 = 5
  Profile = -> Sketch182
  ReferenceAxis = -> Sketch182 [N_Axis]
  Refine = true
  Suppressed = false
  Type = 0
FEATURE [Sketcher::SketchObject] Sketch183
  ArcFitTolerance = 1e-06
  AttachmentSupport = -> [Pocket008]
  ExternalGeometry = -> [Pocket008]
  FullyConstrained = true
  MakeInternals = false
  MapMode = 5
  Placement = pos=(0,0,7.2) rot=(0,0,1;0rad)
  sketch-geometry (4):
    g0: LineSegment StartX=12.2585 StartY=16.4 StartZ=0 EndX=15.2585 EndY=16.4 EndZ=0
    g1: LineSegment StartX=12.2585 StartY=16.4 StartZ=0 EndX=11.7585 EndY=13.5 EndZ=0
    g2: LineSegment StartX=11.7585 StartY=13.5 StartZ=0 EndX=15.2585 EndY=13.5 EndZ=0
    g3: LineSegment StartX=15.2585 StartY=16.4 StartZ=0 EndX=15.2585 EndY=13.5 EndZ=0
  constraints (9):
    c: Coincident(g0,g-4)
    c: Coincident(g0,g-3)
    c: Coincident(g1,g0)
    c: Coincident(g1,g-4)
    c: Coincident(g2,g1)
    c: Horizontal(g2)
    c: Coincident(g3,g0)
    c: Coincident(g3,g2)
    c: Vertical(g3)
FEATURE [PartDesign::Pocket] Pocket009
  BaseFeature = -> Pocket008
  Direction = (0,0,-1)
  Length = 1.95
  Length2 = 5
  Profile = -> Sketch183
  ReferenceAxis = -> Sketch183 [N_Axis]
  Refine = true
  Suppressed = false
  Type = 0
FEATURE [Sketcher::SketchObject] Sketch184
  ArcFitTolerance = 1e-06
  AttachmentSupport = -> [Pocket009]
  ExternalGeometry = -> [Pocket009]
  FullyConstrained = true
  MakeInternals = false
  MapMode = 5
  Placement = pos=(18.2585,-6.9209e-12,-6.8795e-12) rot=(0.57735,0.57735,0.57735;2.0944rad)
  sketch-geometry (6):
    g0: LineSegment StartX=13.5 StartY=7.2 StartZ=0 EndX=17.9 EndY=7.2 EndZ=0
    g1: LineSegment StartX=17.9 StartY=6.5 StartZ=0 EndX=13.5 EndY=7.2 EndZ=0
    g2: LineSegment StartX=13.5 StartY=0.3 StartZ=0 EndX=17.9 EndY=0.3 EndZ=0
    g3: LineSegment StartX=17.9 StartY=0.3 StartZ=0 EndX=17.9 EndY=1 EndZ=0
    g4: LineSegment StartX=17.9 StartY=1 StartZ=0 EndX=13.5 EndY=0.3 EndZ=0
    g5: LineSegment StartX=17.9 StartY=7.2 StartZ=0 EndX=17.9 EndY=6.5 EndZ=0
  constraints (15):
    c: DistanceY(g-4,g-4) = 6.9
    c: Coincident(g0,g-6)
    c: Coincident(g0,g-4)
    c: PointOnObject(g1,g-4)
    c: Coincident(g1,g0)
    c: Coincident(g2,g-5)
    c: Coincident(g2,g-4)
    c: Coincident(g3,g2)
    c: PointOnObject(g3,g-4)
    c: Coincident(g4,g2)
    c: DistanceY(g4,g1) = 5.5
    c: DistanceY(g3,g3) = 0.7
    c: Coincident(g4,g3)
    c: Coincident(g5,g0)
    c: Coincident(g5,g1)
FEATURE [PartDesign::Pocket] Pocket010
  BaseFeature = -> Pocket009
  Direction = (-1,3.79e-13,3.768e-13)
  Length = 5
  Length2 = 5
  Profile = -> Sketch184
  ReferenceAxis = -> Sketch184 [N_Axis]
  Refine = true
  Suppressed = false
  Type = 0
FEATURE [Sketcher::SketchObject] Sketch185
  ArcFitTolerance = 1e-06
  AttachmentSupport = -> [Pocket010]
  ExternalGeometry = -> [Pocket010]
  FullyConstrained = true
  MakeInternals = false
  MapMode = 5
  Placement = pos=(0,0,7.2) rot=(0,0,1;0rad)
  sketch-geometry (4):
    g0: LineSegment StartX=7.8359 StartY=6 StartZ=0 EndX=13.7168 EndY=6 EndZ=0
    g1: LineSegment StartX=10.1453 StartY=2 StartZ=0 EndX=16.1978 EndY=2 EndZ=0
    g2: ArcOfCircle CenterX=17.3282 CenterY=5.47056 CenterZ=0 NormalX=0 NormalY=0 NormalZ=1 AngleXU=0 Radius=3.65 StartAngle=2.99603 EndAngle=4.39753
    g3: LineSegment StartX=7.8359 StartY=6 StartZ=0 EndX=10.1453 EndY=2 EndZ=0
  constraints (13):
    c: PointOnObject(g0,g-4)
    c: PointOnObject(g0,g-3)
    c: Horizontal(g0)
    c: PointOnObject(g1,g-4)
    c: PointOnObject(g1,g-3)
    c: Horizontal(g1)
    c: PointOnObject(g2,g0)
    c: Coincident(g2,g1)
    c: Coincident(g3,g0)
    c: Coincident(g3,g1)
    c: DistanceY(g-5,g0) = 0
    c: DistanceY(g1,g3) = 4
    c: Tangent(g2,g-3) = -1.5708
FEATURE [PartDesign::Pocket] Pocket011
  BaseFeature = -> Pocket010
  Direction = (0,0,-1)
  Length = 1.9
  Length2 = 5
  Profile = -> Sketch185
  ReferenceAxis = -> Sketch185 [N_Axis]
  Refine = true
  Suppressed = false
  Type = 0
FEATURE [Sketcher::SketchObject] Sketch186
  ArcFitTolerance = 1e-06
  AttachmentSupport = -> [Pocket011]
  ExternalGeometry = -> [Pocket011]
  FullyConstrained = true
  MakeInternals = false
  MapMode = 5
  Placement = pos=(0,0,0.3) rot=(1,0,0;3.14159rad)
  sketch-geometry (4):
    g0: ArcOfCircle CenterX=17.3282 CenterY=-5.47056 CenterZ=0 NormalX=0 NormalY=0 NormalZ=1 AngleXU=0 Radius=3.65 StartAngle=1.88566 EndAngle=3.28716
    g1: LineSegment StartX=7.8359 StartY=-6 StartZ=0 EndX=10.1453 EndY=-2 EndZ=0
    g2: LineSegment StartX=10.1453 StartY=-2 StartZ=0 EndX=16.1978 EndY=-2 EndZ=0
    g3: LineSegment StartX=13.7168 StartY=-6 StartZ=0 EndX=7.8359 EndY=-6 EndZ=0
  constraints (12):
    c: Tangent(g0,g-4) = -1.5708
    c: PointOnObject(g0,g-4)
    c: PointOnObject(g1,g-3)
    c: PointOnObject(g1,g-3)
    c: Coincident(g2,g1)
    c: Coincident(g2,g0)
    c: Horizontal(g2)
    c: Coincident(g3,g0)
    c: Coincident(g3,g1)
    c: Horizontal(g3)
    c: DistanceY(g-5,g1) = 0
    c: DistanceY(g1,g1) = 4
FEATURE [PartDesign::Pocket] Pocket012
  BaseFeature = -> Pocket011
  Direction = (0,0,1)
  Length = 1.9
  Length2 = 5
  Profile = -> Sketch186
  ReferenceAxis = -> Sketch186 [N_Axis]
  Refine = true
  Suppressed = false
  Type = 0
FEATURE [Sketcher::SketchObject] Sketch187
  ArcFitTolerance = 1e-06
  AttachmentSupport = -> [Pocket012]
  ExternalGeometry = -> [Pocket012]
  FullyConstrained = true
  MakeInternals = false
  MapMode = 5
  Placement = pos=(0,0,7.2) rot=(0,0,1;0rad)
  sketch-geometry (4):
    g0: LineSegment StartX=7.25855 StartY=7 StartZ=0 EndX=9.65855 EndY=7 EndZ=0
    g1: LineSegment StartX=9.65855 StartY=7 StartZ=0 EndX=9.65855 EndY=13.5 EndZ=0
    g2: LineSegment StartX=9.65855 StartY=13.5 StartZ=0 EndX=7.25855 EndY=13.5 EndZ=0
    g3: LineSegment StartX=7.25855 StartY=13.5 StartZ=0 EndX=7.25855 EndY=7 EndZ=0
  constraints (10):
    c: Coincident(g0,g-4)
    c: Horizontal(g0)
    c: Coincident(g1,g0)
    c: PointOnObject(g1,g-3)
    c: Vertical(g1)
    c: Coincident(g2,g1)
    c: Coincident(g2,g-4)
    c: Coincident(g3,g2)
    c: Coincident(g3,g0)
    c: DistanceX(g2,g2) = 2.4
FEATURE [PartDesign::Pocket] Pocket013
  BaseFeature = -> Pocket012
  Direction = (0,0,-1)
  Length = 0.5
  Length2 = 5
  Profile = -> Sketch187
  ReferenceAxis = -> Sketch187 [N_Axis]
  Refine = true
  Suppressed = false
  Type = 0
FEATURE [Sketcher::SketchObject] Sketch188
  ArcFitTolerance = 1e-06
  AttachmentSupport = -> [Pocket013]
  ExternalGeometry = -> [Pocket013]
  FullyConstrained = true
  MakeInternals = false
  MapMode = 5
  Placement = pos=(0,0,0.3) rot=(1,0,0;3.14159rad)
  sketch-geometry (4):
    g0: LineSegment StartX=7.25855 StartY=-7 StartZ=0 EndX=7.25855 EndY=-13.5 EndZ=0
    g1: LineSegment StartX=7.25855 StartY=-13.5 StartZ=0 EndX=9.65855 EndY=-13.5 EndZ=0
    g2: LineSegment StartX=9.65855 StartY=-13.5 StartZ=0 EndX=9.65855 EndY=-7 EndZ=0
    g3: LineSegment StartX=7.25855 StartY=-7 StartZ=0 EndX=9.65855 EndY=-7 EndZ=0
  constraints (10):
    c: Coincident(g0,g-3)
    c: Coincident(g0,g-4)
    c: Coincident(g1,g0)
    c: PointOnObject(g1,g-4)
    c: Coincident(g2,g1)
    c: Vertical(g2)
    c: Coincident(g3,g0)
    c: Coincident(g3,g2)
    c: Horizontal(g3)
    c: DistanceX(g1,g1) = 2.4
FEATURE [PartDesign::Pocket] Pocket014
  BaseFeature = -> Pocket013
  Direction = (0,0,1)
  Length = 0.5
  Length2 = 5
  Profile = -> Sketch188
  ReferenceAxis = -> Sketch188 [N_Axis]
  Refine = true
  Suppressed = false
  Type = 0
FEATURE [Sketcher::SketchObject] Sketch189
  ArcFitTolerance = 1e-06
  AttachmentSupport = -> [Pocket014]
  ExternalGeometry = -> [Pocket014]
  FullyConstrained = true
  MakeInternals = false
  MapMode = 5
  Placement = pos=(0,0,7.2) rot=(0,0,1;0rad)
  sketch-geometry (4):
    g0: LineSegment StartX=9.65855 StartY=7 StartZ=0 EndX=7.25855 EndY=7 EndZ=0
    g1: LineSegment StartX=7.25855 StartY=7 StartZ=0 EndX=7.8359 EndY=6 EndZ=0
    g2: LineSegment StartX=7.8359 StartY=6 StartZ=0 EndX=9.65855 EndY=6 EndZ=0
    g3: LineSegment StartX=9.65855 StartY=7 StartZ=0 EndX=9.65855 EndY=6 EndZ=0
  constraints (9):
    c: Coincident(g0,g-3)
    c: Coincident(g0,g-4)
    c: Coincident(g1,g-4)
    c: Coincident(g1,g-5)
    c: Coincident(g2,g-5)
    c: PointOnObject(g2,g-5)
    c: Coincident(g3,g0)
    c: Coincident(g3,g2)
    c: Vertical(g3)
FEATURE [PartDesign::Pocket] Pocket015
  BaseFeature = -> Pocket014
  Direction = (0,0,-1)
  Length = 0.3
  Length2 = 5
  Profile = -> Sketch189
  ReferenceAxis = -> Sketch189 [N_Axis]
  Refine = true
  Suppressed = false
  Type = 0
FEATURE [Sketcher::SketchObject] Sketch190
  ArcFitTolerance = 1e-06
  AttachmentSupport = -> [Pocket015]
  ExternalGeometry = -> [Pocket015]
  FullyConstrained = true
  MakeInternals = false
  MapMode = 5
  Placement = pos=(0,0,0.3) rot=(1,0,0;3.14159rad)
  sketch-geometry (4):
    g0: LineSegment StartX=9.65855 StartY=-7 StartZ=0 EndX=7.25855 EndY=-7 EndZ=0
    g1: LineSegment StartX=7.25855 StartY=-7 StartZ=0 EndX=7.8359 EndY=-6 EndZ=0
    g2: LineSegment StartX=7.8359 StartY=-6 StartZ=0 EndX=9.65855 EndY=-6 EndZ=0
    g3: LineSegment StartX=9.65855 StartY=-7 StartZ=0 EndX=9.65855 EndY=-6 EndZ=0
  constraints (9):
    c: Coincident(g0,g-5)
    c: Coincident(g0,g-5)
    c: Coincident(g1,g-5)
    c: Coincident(g1,g-4)
    c: PointOnObject(g2,g-4)
    c: Coincident(g3,g0)
    c: Coincident(g3,g2)
    c: Vertical(g3)
    c: Coincident(g2,g1)
FEATURE [PartDesign::Pocket] Pocket016
  BaseFeature = -> Pocket015
  Direction = (0,0,1)
  Length = 0.3
  Length2 = 5
  Profile = -> Sketch190
  ReferenceAxis = -> Sketch190 [N_Axis]
  Refine = true
  Suppressed = false
  Type = 0
FEATURE [Sketcher::SketchObject] Sketch191
  ArcFitTolerance = 1e-06
  AttachmentSupport = -> [Pocket016]
  ExternalGeometry = -> [Pocket016]
  FullyConstrained = true
  MakeInternals = false
  MapMode = 5
  Placement = pos=(0,0,7.2) rot=(0,0,1;0rad)
  sketch-geometry (12):
    g0: LineSegment StartX=11.5113 StartY=1.7 StartZ=0 EndX=11.5113 EndY=-0.5 EndZ=0
    g1: LineSegment StartX=11.8113 StartY=-0.8 StartZ=0 EndX=15.0113 EndY=-0.8 EndZ=0
    g2: LineSegment StartX=15.3113 StartY=-0.5 StartZ=0 EndX=15.3113 EndY=1.7 EndZ=0
    g3: LineSegment StartX=15.0113 StartY=2 StartZ=0 EndX=11.8113 EndY=2 EndZ=0
    g4: ArcOfCircle CenterX=15.0113 CenterY=1.7 CenterZ=0 NormalX=0 NormalY=0 NormalZ=1 AngleXU=0 Radius=0.3 StartAngle=1e-16 EndAngle=1.5708
    g5: GeomPoint [constr] X=15.3113 Y=2 Z=0
    g6: ArcOfCircle CenterX=11.8113 CenterY=1.7 CenterZ=0 NormalX=0 NormalY=0 NormalZ=1 AngleXU=0 Radius=0.3 StartAngle=1.5708 EndAngle=3.14159
    g7: GeomPoint [constr] X=11.5113 Y=2 Z=0
    g8: ArcOfCircle CenterX=11.8113 CenterY=-0.5 CenterZ=0 NormalX=0 NormalY=0 NormalZ=1 AngleXU=0 Radius=0.3 StartAngle=3.14159 EndAngle=4.71239
    g9: GeomPoint [constr] X=11.5113 Y=-0.8 Z=0
    g10: ArcOfCircle CenterX=15.0113 CenterY=-0.5 CenterZ=0 NormalX=0 NormalY=0 NormalZ=1 AngleXU=0 Radius=0.3 StartAngle=4.71239 EndAngle=6.28319
    g11: GeomPoint [constr] X=15.3113 Y=-0.8 Z=0
  constraints (28):
    c: Vertical(g0)
    c: Vertical(g2)
    c: Horizontal(g1)
    c: Horizontal(g3)
    c: PointOnObject(g5,g2)
    c: PointOnObject(g5,g3)
    c: Tangent(g2,g4) = -1.5708
    c: Tangent(g3,g4) = -1.5708
    c: PointOnObject(g7,g0)
    c: PointOnObject(g7,g3)
    c: Tangent(g0,g6) = -1.5708
    c: Tangent(g3,g6) = -1.5708
    c: PointOnObject(g9,g0)
    c: PointOnObject(g9,g1)
    c: Tangent(g0,g8) = -1.5708
    c: Tangent(g1,g8) = -1.5708
    c: PointOnObject(g11,g1)
    c: PointOnObject(g11,g2)
    c: Tangent(g1,g10) = -1.5708
    c: Tangent(g2,g10) = -1.5708
    c: Radius(g6) = 0.3
    c: Radius(g4) = 0.3
    c: Radius(g10) = 0.3
    c: Radius(g8) = 0.3
    c: DistanceY(g1,g3) = 2.8
    c: DistanceX(g0,g2) = 3.8
    c: PointOnObject(g3,g-4)
    c: DistanceX(g-5,g0) = 0.5
FEATURE [PartDesign::Pad] Pad138
  BaseFeature = -> Pocket016
  Direction = (0,0,1)
  Length = 0.65
  Length2 = 10
  Profile = -> Sketch191
  ReferenceAxis = -> Sketch191 [N_Axis]
  Refine = true
  Suppressed = false
  Type = 0
FEATURE [PartDesign::Body] Body018  label="Devastator_Gun"
  AllowCompound = false
  Group = -> [Sketch171,Pad134,Sketch172,Pocket002,Sketch173,Pocket003,Sketch174,Pad135,Sketch175,Pocket004,Sketch176,Pocket005,Sketch177,Pad136,Sketch178,Pad137,Sketch179,Sketch180,Pocket006,Sketch181,Pocket007,Sketch182,Pocket008,Sketch183,Pocket009,Sketch184,Pocket010,Sketch185,Pocket011,Sketch186,Pocket012,Sketch187,Pocket013,Sketch188,Pocket014,Sketch189,Pocket015,Sketch190,Pocket016,Sketch191,Pad138,+75 more]
  Origin = -> Origin020
  Placement = pos=(-48.8,-0.5,23.8) rot=(1,0,0;1.5708rad)
  Tip = -> Pocket027
COMPONENT P2 — recipe-attached ("Mixmaster_Gun", modeled in this document).
Construction recipe (the document's own serialized feature program — sketch geometry with constraints, then the solid features built on it; lengths are millimeters unless a unit is written):

FEATURE [Sketcher::SketchObject] Sketch225
  ArcFitTolerance = 1e-06
  AttachmentSupport = -> [XZ_Plane021]
  FullyConstrained = true
  MakeInternals = false
  MapMode = 5
  Placement = pos=(0,0,0) rot=(1,0,0;1.5708rad)
  sketch-geometry (15):
    g0: LineSegment StartX=0 StartY=0 StartZ=0 EndX=6 EndY=0 EndZ=0
    g1: LineSegment StartX=6 StartY=0 StartZ=0 EndX=6.7 EndY=-1 EndZ=0
    g2: LineSegment StartX=6.7 StartY=-1 StartZ=0 EndX=14.2 EndY=-1 EndZ=0
    g3: LineSegment StartX=14.2 StartY=-1 StartZ=0 EndX=14.2 EndY=6 EndZ=0
    g4: LineSegment StartX=14.2 StartY=6 StartZ=0 EndX=13.4 EndY=6.8 EndZ=0
    g5: LineSegment StartX=13.4 StartY=6.8 StartZ=0 EndX=11.9 EndY=6.8 EndZ=0
    g6: LineSegment StartX=11.9 StartY=6.8 StartZ=0 EndX=11.9 EndY=7.8 EndZ=0
    g7: LineSegment StartX=11.9 StartY=7.8 StartZ=0 EndX=8.4 EndY=7.8 EndZ=0
    g8: LineSegment StartX=8.4 StartY=7.8 StartZ=0 EndX=7.93369 EndY=6.8 EndZ=0
    g9: LineSegment StartX=7.93369 StartY=6.8 StartZ=0 EndX=4.5 EndY=6.8 EndZ=0
    g10: LineSegment StartX=4.5 StartY=6.8 StartZ=0 EndX=3.5 EndY=5.8 EndZ=0
    g11: LineSegment StartX=3.5 StartY=5.8 StartZ=0 EndX=-2.5 EndY=5.8 EndZ=0
    g12: LineSegment StartX=-2.5 StartY=5.8 StartZ=0 EndX=-2.5 EndY=1.3 EndZ=0
    g13: LineSegment StartX=-2.5 StartY=1.3 StartZ=0 EndX=0 EndY=1.3 EndZ=0
    g14: LineSegment StartX=0 StartY=1.3 StartZ=0 EndX=0 EndY=0 EndZ=0
  constraints (44):
    c: PointOnObject(g0,g-1)
    c: Coincident(g1,g0)
    c: Coincident(g2,g1)
    c: Horizontal(g2)
    c: DistanceX(g2,g2) = 7.5
    c: Coincident(g3,g2)
    c: Vertical(g3)
    c: Coincident(g4,g3)
    c: Coincident(g5,g4)
    c: Horizontal(g5)
    c: Coincident(g6,g5)
    c: Vertical(g6)
    c: Coincident(g7,g6)
    c: Horizontal(g7)
    c: Coincident(g8,g7)
    c: Coincident(g9,g8)
    c: Horizontal(g9)
    c: Coincident(g10,g9)
    c: Coincident(g11,g10)
    c: Horizontal(g11)
    c: Coincident(g12,g11)
    c: Vertical(g12)
    c: Coincident(g13,g12)
    c: Horizontal(g13)
    c: Coincident(g14,g13)
    c: Coincident(g14,g0)
    c: Vertical(g14)
    c: DistanceY(g3,g3) = 7
    c: DistanceX(g7,g7) = 3.5
    c: DistanceX(g0,g2) = 14.2
    c: DistanceX(g13,g13) = 2.5
    c: DistanceY(g6,g6) = 1
    c: DistanceY(g8,g7) = 1
    c: DistanceY(g2,g6) = 8.8
    c: DistanceX(g11,g11) = 6
    c: DistanceX(g0,g0) = 6
    c: DistanceY(g1,g0) = 1
    c: Angle(g8,g7) = 2.00713
    c: Angle(g10,g9) = 2.35619
    c: Angle(g4,g3) = 2.35619
    c: DistanceY(g12,g12) = 4.5
    c: DistanceY(g10,g9) = 1
    c: DistanceX(g5,g5) = 1.5
    c: Coincident(g0,g-1)
FEATURE [PartDesign::Pad] Pad156
  Direction = (0,-1,2e-16)
  Length = 2.7
  Length2 = 10
  Placement = pos=(0,0,0) rot=(1,0,0;1.5708rad)
  Profile = -> Sketch225
  ReferenceAxis = -> Sketch225 [N_Axis]
  Refine = true
  Suppressed = false
  Type = 0
FEATURE [Sketcher::SketchObject] Sketch226
  ArcFitTolerance = 1e-06
  AttachmentSupport = -> [Pad156]
  ExternalGeometry = -> [Pad156]
  FullyConstrained = true
  MakeInternals = false
  MapMode = 5
  Placement = pos=(-2.5,0,0) rot=(0.707107,0,-0.707107;3.14159rad)
  sketch-geometry (4):
    g0: ArcOfCircle CenterX=-4.2275 CenterY=1.35 CenterZ=0 NormalX=0 NormalY=0 NormalZ=1 AngleXU=0 Radius=2.0725 StartAngle=2.43218 EndAngle=3.851
    g1: LineSegment StartX=-5.8 StartY=4.7957e-12 StartZ=0 EndX=-5.8 EndY=2.7 EndZ=0
    g2: LineSegment [constr] StartX=-6.8 StartY=-1.5e-15 StartZ=0 EndX=-5.8 EndY=4.7957e-12 EndZ=0
    g3: LineSegment [constr] StartX=-6.3 StartY=-1.4e-15 StartZ=0 EndX=-6.3 EndY=2.7 EndZ=0
  constraints (12):
    c: Coincident(g0,g-3)
    c: Coincident(g0,g-3)
    c: Coincident(g1,g0)
    c: Coincident(g1,g0)
    c: Coincident(g2,g-6)
    c: Coincident(g2,g0)
    c: PointOnObject(g3,g2)
    c: Symmetric(g-4,g-4,g3)
    c: Vertical(g3)
    c: DistanceX(g2,g0) = 1
    c: DistanceX(g2,g3) = 0.5
    c: Tangent(g0,g3)
FEATURE [PartDesign::Pad] Pad157
  BaseFeature = -> Pad156
  Direction = (-1,0,-2e-16)
  Length = 6
  Length2 = 10
  Placement = pos=(0,0,0) rot=(1,0,0;1.5708rad)
  Profile = -> Sketch226
  ReferenceAxis = -> Sketch226 [N_Axis]
  Refine = true
  Reversed = true
  Suppressed = false
  Type = 0
FEATURE [Sketcher::SketchObject] Sketch227
  ArcFitTolerance = 1e-06
  AttachmentSupport = -> [Pad157]
  ExternalGeometry = -> [Pad157]
  FullyConstrained = true
  MakeInternals = false
  MapMode = 5
  Placement = pos=(-2.5,0,0) rot=(0.707107,0,-0.707107;3.14159rad)
  sketch-geometry (2):
    g0: ArcOfCircle CenterX=-4.2275 CenterY=1.35 CenterZ=0 NormalX=0 NormalY=0 NormalZ=1 AngleXU=0 Radius=2.5 StartAngle=0.570437 EndAngle=5.71275
    g1: LineSegment StartX=-2.12334 StartY=2.7 StartZ=0 EndX=-2.12334 EndY=-1.3e-15 EndZ=0
  constraints (6):
    c: PointOnObject(g0,g-4)
    c: PointOnObject(g0,g-5)
    c: Diameter(g0) = 5
    c: Coincident(g0,g-3)
    c: Coincident(g1,g0)
    c: Coincident(g1,g0)
FEATURE [PartDesign::Pad] Pad158
  BaseFeature = -> Pad157
  Direction = (-1,0,-2e-16)
  Length = 1.2
  Length2 = 10
  Placement = pos=(0,0,0) rot=(1,0,0;1.5708rad)
  Profile = -> Sketch227
  ReferenceAxis = -> Sketch227 [N_Axis]
  Refine = true
  Reversed = true
  Suppressed = false
  Type = 0
FEATURE [Sketcher::SketchObject] Sketch228
  ArcFitTolerance = 1e-06
  AttachmentOffset = pos=(0,0,1) rot=(0,0,1;0rad)
  AttachmentSupport = -> [Pad158]
  ExternalGeometry = -> [Pad158]
  FullyConstrained = true
  MakeInternals = false
  MapMode = 5
  Placement = pos=(-0.3,0,-5e-16) rot=(0.707107,0,0.707107;3.14159rad)
  sketch-geometry (2):
    g0: ArcOfCircle CenterX=4.2275 CenterY=1.35 CenterZ=0 NormalX=0 NormalY=0 NormalZ=1 AngleXU=0 Radius=2.5 StartAngle=3.71203 EndAngle=8.85434
    g1: LineSegment StartX=2.12334 StartY=2.7 StartZ=0 EndX=2.12334 EndY=0 EndZ=0
  constraints (4):
    c: Tangent(g0,g-3) = -1.5708
    c: Coincident(g0,g-3)
    c: Coincident(g1,g0)
    c: Coincident(g1,g-3)
FEATURE [PartDesign::Pad] Pad159
  BaseFeature = -> Pad158
  Direction = (1,0,-2e-16)
  Length = 2.7
  Length2 = 10
  Placement = pos=(0,0,0) rot=(1,0,0;1.5708rad)
  Profile = -> Sketch228
  ReferenceAxis = -> Sketch228 [N_Axis]
  Refine = true
  Suppressed = false
  Type = 0
FEATURE [Sketcher::SketchObject] Sketch229
  ArcFitTolerance = 1e-06
  AttachmentSupport = -> [Pad159]
  ExternalGeometry = -> [Pad159]
  FullyConstrained = true
  MakeInternals = false
  MapMode = 5
  Placement = pos=(-2.5,0,-7e-16) rot=(0.707107,0,-0.707107;3.14159rad)
  sketch-geometry (1):
    g0: Circle CenterX=-4.2275 CenterY=1.35 CenterZ=0 NormalX=0 NormalY=0 NormalZ=1 AngleXU=0 Radius=1
  constraints (2):
    c: Coincident(g0,g-3)
    c: Diameter(g0) = 2
FEATURE [PartDesign::Pad] Pad160
  BaseFeature = -> Pad159
  Direction = (-1,0,-2e-16)
  Length = 1
  Length2 = 10
  Placement = pos=(0,0,0) rot=(1,0,0;1.5708rad)
  Profile = -> Sketch229
  ReferenceAxis = -> Sketch229 [N_Axis]
  Refine = true
  Suppressed = false
  Type = 0
FEATURE [Sketcher::SketchObject] Sketch230
  ArcFitTolerance = 1e-06
  AttachmentSupport = -> [Pad160]
  ExternalGeometry = -> [Pad160]
  FullyConstrained = true
  MakeInternals = false
  MapMode = 5
  Placement = pos=(-3.5,0,0) rot=(0.707107,0,-0.707107;3.14159rad)
  sketch-geometry (1):
    g0: Circle CenterX=-4.2275 CenterY=1.35 CenterZ=0 NormalX=0 NormalY=0 NormalZ=1 AngleXU=0 Radius=1.65
  constraints (2):
    c: Coincident(g0,g-3)
    c: Diameter(g0) = 3.3
FEATURE [Sketcher::SketchObject] Sketch231
  ArcFitTolerance = 1e-06
  AttachmentOffset = pos=(0,0,2.3) rot=(0,0,1;0rad)
  AttachmentSupport = -> [Pad160]
  ExternalGeometry = -> [Pad160]
  FullyConstrained = true
  MakeInternals = false
  MapMode = 5
  Placement = pos=(-5.8,0,-5e-16) rot=(0.707107,0,-0.707107;3.14159rad)
  sketch-geometry (1):
    g0: Circle CenterX=-4.2275 CenterY=1.35 CenterZ=0 NormalX=0 NormalY=0 NormalZ=1 AngleXU=0 Radius=1.4
  constraints (2):
    c: Coincident(g0,g-3)
    c: Diameter(g0) = 2.8
FEATURE [PartDesign::AdditiveLoft] AdditiveLoft007
  BaseFeature = -> Pad160
  Closed = false
  Placement = pos=(0,0,0) rot=(1,0,0;1.5708rad)
  Profile = -> Sketch230
  Refine = true
  Ruled = false
  Sections = -> [Sketch231]
  Suppressed = false
FEATURE [Sketcher::SketchObject] Sketch232
  ArcFitTolerance = 1e-06
  AttachmentSupport = -> [AdditiveLoft007]
  ExternalGeometry = -> [AdditiveLoft007]
  FullyConstrained = true
  MakeInternals = false
  MapMode = 5
  Placement = pos=(0,-2.7,0) rot=(1,0,0;1.5708rad)
  sketch-geometry (12):
    g0: LineSegment StartX=3.5 StartY=1 StartZ=0 EndX=3.5 EndY=5.8 EndZ=0
    g1: LineSegment StartX=3.5 StartY=5.8 StartZ=0 EndX=4.5 EndY=6.8 EndZ=0
    g2: LineSegment StartX=4.5 StartY=6.8 StartZ=0 EndX=7.93369 EndY=6.8 EndZ=0
    g3: LineSegment StartX=7.93369 StartY=6.8 StartZ=0 EndX=8.4 EndY=7.8 EndZ=0
    g4: LineSegment StartX=8.4 StartY=7.8 StartZ=0 EndX=11.9 EndY=7.8 EndZ=0
    g5: LineSegment StartX=11.9 StartY=7.8 StartZ=0 EndX=11.9 EndY=6.8 EndZ=0
    g6: LineSegment StartX=11.9 StartY=6.8 StartZ=0 EndX=13.4 EndY=6.8 EndZ=0
    g7: LineSegment StartX=13.4 StartY=6.8 StartZ=0 EndX=14.2 EndY=6 EndZ=0
    g8: LineSegment StartX=14.2 StartY=6 StartZ=0 EndX=14.2 EndY=-1 EndZ=0
    g9: LineSegment StartX=14.2 StartY=-1 StartZ=0 EndX=6.7 EndY=-1 EndZ=0
    g10: LineSegment StartX=6.7 StartY=-1 StartZ=0 EndX=5.3 EndY=1 EndZ=0
    g11: LineSegment StartX=5.3 StartY=1 StartZ=0 EndX=3.5 EndY=1 EndZ=0
  constraints (26):
    c: Coincident(g0,g-5)
    c: Vertical(g0)
    c: Coincident(g1,g0)
    c: Coincident(g1,g-6)
    c: Coincident(g2,g1)
    c: Coincident(g2,g-7)
    c: Coincident(g3,g2)
    c: Coincident(g3,g-8)
    c: Coincident(g4,g3)
    c: Coincident(g4,g-8)
    c: Coincident(g5,g4)
    c: Coincident(g5,g-10)
    c: Coincident(g6,g5)
    c: Coincident(g6,g-11)
    c: Coincident(g7,g6)
    c: Coincident(g7,g-11)
    c: Coincident(g8,g7)
    c: Coincident(g8,g-4)
    c: Coincident(g9,g8)
    c: Coincident(g10,g9)
    c: PointOnObject(g-12,g10)
    c: Coincident(g9,g-12)
    c: Coincident(g11,g10)
    c: Coincident(g11,g0)
    c: Horizontal(g11)
    c: DistanceY(g-12,g10) = 1
FEATURE [PartDesign::Pad] Pad161
  BaseFeature = -> AdditiveLoft007
  Direction = (0,-1,2e-16)
  Length = 0.65
  Length2 = 10
  Placement = pos=(0,0,0) rot=(1,0,0;1.5708rad)
  Profile = -> Sketch232
  ReferenceAxis = -> Sketch232 [N_Axis]
  Refine = true
  Suppressed = false
  Type = 0
FEATURE [Sketcher::SketchObject] Sketch233
  ArcFitTolerance = 1e-06
  AttachmentSupport = -> [Pad161]
  ExternalGeometry = -> [Pad161]
  FullyConstrained = true
  MakeInternals = false
  MapMode = 5
  Placement = pos=(0,7e-16,0) rot=(-1,0,0;1.5708rad)
  sketch-geometry (12):
    g0: LineSegment StartX=6.7 StartY=1 StartZ=0 EndX=5.3 EndY=-1 EndZ=0
    g1: LineSegment StartX=5.3 StartY=-1 StartZ=0 EndX=3.5 EndY=-1 EndZ=0
    g2: LineSegment StartX=3.5 StartY=-5.8 StartZ=0 EndX=3.5 EndY=-1 EndZ=0
    g3: LineSegment StartX=6.7 StartY=1 StartZ=0 EndX=14.2 EndY=1 EndZ=0
    g4: LineSegment StartX=14.2 StartY=1 StartZ=0 EndX=14.2 EndY=-6 EndZ=0
    g5: LineSegment StartX=14.2 StartY=-6 StartZ=0 EndX=13.4 EndY=-6.8 EndZ=0
    g6: LineSegment StartX=13.4 StartY=-6.8 StartZ=0 EndX=11.9 EndY=-6.8 EndZ=0
    g7: LineSegment StartX=11.9 StartY=-6.8 StartZ=0 EndX=11.9 EndY=-7.8 EndZ=0
    g8: LineSegment StartX=11.9 StartY=-7.8 StartZ=0 EndX=8.4 EndY=-7.8 EndZ=0
    g9: LineSegment StartX=8.4 StartY=-7.8 StartZ=0 EndX=7.93369 EndY=-6.8 EndZ=0
    g10: LineSegment StartX=7.93369 StartY=-6.8 StartZ=0 EndX=4.5 EndY=-6.8 EndZ=0
    g11: LineSegment StartX=4.5 StartY=-6.8 StartZ=0 EndX=3.5 EndY=-5.8 EndZ=0
  constraints (26):
    c: Coincident(g0,g-4)
    c: PointOnObject(g-3,g0)
    c: Coincident(g1,g0)
    c: Horizontal(g1)
    c: Coincident(g2,g-12)
    c: Coincident(g2,g1)
    c: Vertical(g2)
    c: DistanceY(g0,g-3) = 1
    c: Coincident(g3,g0)
    c: Coincident(g3,g-5)
    c: Coincident(g4,g3)
    c: Coincident(g4,g-6)
    c: Coincident(g5,g4)
    c: Coincident(g5,g-7)
    c: Coincident(g6,g5)
    c: Coincident(g6,g-8)
    c: Coincident(g7,g6)
    c: Coincident(g7,g-9)
    c: Coincident(g8,g7)
    c: Coincident(g8,g-10)
    c: Coincident(g9,g8)
    c: Coincident(g9,g-11)
    c: Coincident(g10,g9)
    c: Coincident(g10,g-12)
    c: Coincident(g11,g10)
    c: Coincident(g11,g2)
FEATURE [PartDesign::Pad] Pad162
  BaseFeature = -> Pad161
  Direction = (0,1,2e-16)
  Length = 0.65
  Length2 = 10
  Placement = pos=(0,0,0) rot=(1,0,0;1.5708rad)
  Profile = -> Sketch233
  ReferenceAxis = -> Sketch233 [N_Axis]
  Refine = true
  Suppressed = false
  Type = 0
FEATURE [Sketcher::SketchObject] Sketch234
  ArcFitTolerance = 1e-06
  AttachmentSupport = -> [Pad162]
  ExternalGeometry = -> [Pad162]
  FullyConstrained = true
  MakeInternals = false
  MapMode = 5
  Placement = pos=(14.2,1.79e-14,0) rot=(0.707107,0,0.707107;3.14159rad)
  sketch-geometry (6):
    g0: LineSegment StartX=2.5 StartY=3.35 StartZ=0 EndX=7.8 EndY=2.7 EndZ=0
    g1: LineSegment StartX=7.8 StartY=1.6e-14 StartZ=0 EndX=2.5 EndY=-0.65 EndZ=0
    g2: LineSegment StartX=7.8 StartY=1.6e-14 StartZ=0 EndX=7.8 EndY=-0.65 EndZ=0
    g3: LineSegment StartX=7.8 StartY=-0.65 StartZ=0 EndX=2.5 EndY=-0.65 EndZ=0
    g4: LineSegment StartX=7.8 StartY=2.7 StartZ=0 EndX=7.8 EndY=3.35 EndZ=0
    g5: LineSegment StartX=2.5 StartY=3.35 StartZ=0 EndX=7.8 EndY=3.35 EndZ=0
  constraints (17):
    c: DistanceY(g-10,g-10) = 4
    c: PointOnObject(g0,g-5)
    c: PointOnObject(g0,g-9)
    c: PointOnObject(g1,g-9)
    c: DistanceX(g-10,g0) = 3.5
    c: DistanceY(g0,g-9) = 0.65
    c: DistanceY(g-9,g1) = 0.65
    c: PointOnObject(g1,g-8)
    c: Coincident(g2,g-9)
    c: Coincident(g3,g2)
    c: Coincident(g3,g1)
    c: Coincident(g4,g0)
    c: Coincident(g5,g0)
    c: Coincident(g5,g4)
    c: Coincident(g2,g1)
    c: Coincident(g4,g-9)
    c: DistanceX(g-10,g1) = 3.5
FEATURE [PartDesign::Pocket] Pocket028
  BaseFeature = -> Pad162
  Direction = (-1,-1.3e-15,2e-16)
  Length = 11
  Length2 = 5
  Placement = pos=(0,0,0) rot=(1,0,0;1.5708rad)
  Profile = -> Sketch234
  ReferenceAxis = -> Sketch234 [N_Axis]
  Refine = true
  Suppressed = false
  Type = 0
FEATURE [Sketcher::SketchObject] Sketch235
  ArcFitTolerance = 1e-06
  AttachmentSupport = -> [Pocket028]
  ExternalGeometry = -> [Pocket028]
  FullyConstrained = true
  MakeInternals = false
  MapMode = 5
  Placement = pos=(0,0.65,0) rot=(-1,0,0;1.5708rad)
  sketch-geometry (4):
    g0: ArcOfCircle CenterX=4.6 CenterY=-2 CenterZ=0 NormalX=0 NormalY=0 NormalZ=1 AngleXU=0 Radius=0.5 StartAngle=1.5708 EndAngle=4.71239
    g1: ArcOfCircle CenterX=13.1 CenterY=-2 CenterZ=0 NormalX=0 NormalY=0 NormalZ=1 AngleXU=0 Radius=0.5 StartAngle=4.71239 EndAngle=7.85398
    g2: LineSegment StartX=4.6 StartY=-1.5 StartZ=0 EndX=13.1 EndY=-1.5 EndZ=0
    g3: LineSegment StartX=4.6 StartY=-2.5 StartZ=0 EndX=13.1 EndY=-2.5 EndZ=0
  constraints (11):
    c: Tangent(g0,g2) = 1.5708
    c: Tangent(g0,g3) = -1.5708
    c: Tangent(g1,g2) = 1.5708
    c: Tangent(g1,g3) = -1.5708
    c: Equal(g0,g1)
    c: Horizontal(g2)
    c: Diameter(g0) = 1
    c: PointOnObject(g0,g-3)
    c: DistanceX(g0,g1) = 8.5
    c: DistanceX(g-5,g-4) = 10.7
    c: DistanceX(g-5,g0) = 1.1
FEATURE [PartDesign::Pad] Pad163
  BaseFeature = -> Pocket028
  Direction = (0,1,2e-16)
  Length = 1
  Length2 = 10
  Placement = pos=(0,0,0) rot=(1,0,0;1.5708rad)
  Profile = -> Sketch235
  ReferenceAxis = -> Sketch235 [N_Axis]
  Refine = true
  Suppressed = false
  Type = 0
FEATURE [Sketcher::SketchObject] Sketch236
  ArcFitTolerance = 1e-06
  AttachmentSupport = -> [Pad163]
  ExternalGeometry = -> [Pad163]
  FullyConstrained = true
  MakeInternals = false
  MapMode = 5
  Placement = pos=(0,-3.35,0) rot=(1,0,0;1.5708rad)
  sketch-geometry (4):
    g0: ArcOfCircle CenterX=4.6 CenterY=2 CenterZ=0 NormalX=0 NormalY=0 NormalZ=1 AngleXU=0 Radius=0.5 StartAngle=1.5708 EndAngle=4.71239
    g1: ArcOfCircle CenterX=13.1 CenterY=2 CenterZ=0 NormalX=0 NormalY=0 NormalZ=1 AngleXU=0 Radius=0.5 StartAngle=4.71239 EndAngle=7.85398
    g2: LineSegment StartX=4.6 StartY=2.5 StartZ=0 EndX=13.1 EndY=2.5 EndZ=0
    g3: LineSegment StartX=4.6 StartY=1.5 StartZ=0 EndX=13.1 EndY=1.5 EndZ=0
  constraints (10):
    c: Tangent(g0,g2) = 1.5708
    c: Tangent(g0,g3) = -1.5708
    c: Tangent(g1,g2) = 1.5708
    c: Tangent(g1,g3) = -1.5708
    c: Equal(g0,g1)
    c: Horizontal(g2)
    c: Diameter(g0) = 1
    c: DistanceX(g0,g1) = 8.5
    c: PointOnObject(g0,g-3)
    c: DistanceX(g1,g-5) = 1.1
FEATURE [PartDesign::Pad] Pad164
  BaseFeature = -> Pad163
  Direction = (0,-1,2e-16)
  Length = 1
  Length2 = 10
  Placement = pos=(0,0,0) rot=(1,0,0;1.5708rad)
  Profile = -> Sketch236
  ReferenceAxis = -> Sketch236 [N_Axis]
  Refine = true
  Suppressed = false
  Type = 0
FEATURE [Sketcher::SketchObject] Sketch237
  ArcFitTolerance = 1e-06
  AttachmentSupport = -> [Pad164]
  ExternalGeometry = -> [Pad164]
  FullyConstrained = true
  MakeInternals = false
  MapMode = 5
  Placement = pos=(0,0,0) rot=(1,0,0;3.14159rad)
  sketch-geometry (1):
    g0: Circle CenterX=3 CenterY=1.35 CenterZ=0 NormalX=0 NormalY=0 NormalZ=1 AngleXU=0 Radius=1.7
  constraints (4):
    c: Diameter(g0) = 3.4
    c: DistanceY(g-4,g-4) = 2.7
    c: DistanceY(g0,g-4) = 1.35
    c: DistanceX(g0,g-4) = 3
FEATURE [PartDesign::Pad] Pad165
  BaseFeature = -> Pad164
  Direction = (0,0,-1)
  Length = 2
  Length2 = 10
  Placement = pos=(0,0,0) rot=(1,0,0;1.5708rad)
  Profile = -> Sketch237
  ReferenceAxis = -> Sketch237 [N_Axis]
  Refine = true
  Suppressed = false
  Type = 0
FEATURE [Sketcher::SketchObject] Sketch238
  ArcFitTolerance = 1e-06
  AttachmentSupport = -> [Pad165]
  ExternalGeometry = -> [Pad165]
  FullyConstrained = true
  MakeInternals = false
  MapMode = 5
  Placement = pos=(0,0,-2) rot=(1,0,0;3.14159rad)
  sketch-geometry (4):
    g0: ArcOfCircle CenterX=3 CenterY=1.35001 CenterZ=0 NormalX=0 NormalY=0 NormalZ=1 AngleXU=0 Radius=1.69999 StartAngle=0.91755 EndAngle=2.22404
    g1: ArcOfCircle CenterX=3 CenterY=1.34999 CenterZ=0 NormalX=0 NormalY=0 NormalZ=1 AngleXU=0 Radius=1.69999 StartAngle=4.05914 EndAngle=5.36563
    g2: LineSegment StartX=1.9668 StartY=2.7 StartZ=0 EndX=4.0332 EndY=2.7 EndZ=0
    g3: LineSegment StartX=1.9668 StartY=-5.9113e-12 StartZ=0 EndX=4.0332 EndY=-5.9115e-12 EndZ=0
  constraints (10):
    c: Coincident(g0,g-5)
    c: Coincident(g0,g-4)
    c: Coincident(g1,g-6)
    c: Coincident(g1,g-7)
    c: Coincident(g2,g0)
    c: Coincident(g2,g0)
    c: Coincident(g3,g1)
    c: Coincident(g3,g1)
    c: Tangent(g0,g-3)
    c: Tangent(g1,g-3)
FEATURE [PartDesign::Pocket] Pocket029
  BaseFeature = -> Pad165
  Direction = (0,0,1)
  Length = 2
  Length2 = 5
  Placement = pos=(0,0,0) rot=(1,0,0;1.5708rad)
  Profile = -> Sketch238
  ReferenceAxis = -> Sketch238 [N_Axis]
  Refine = true
  Suppressed = false
  Type = 0
FEATURE [Sketcher::SketchObject] Sketch239
  ArcFitTolerance = 1e-06
  AttachmentSupport = -> [Pocket029]
  ExternalGeometry = -> [Pocket029]
  FullyConstrained = true
  MakeInternals = false
  MapMode = 5
  Placement = pos=(0,0,-2) rot=(1,0,0;3.14159rad)
  sketch-geometry (1):
    g0: Circle CenterX=3 CenterY=1.35 CenterZ=0 NormalX=0 NormalY=0 NormalZ=1 AngleXU=0 Radius=1.4
  constraints (2):
    c: Coincident(g0,g-3)
    c: Radius(g0) = 1.4
FEATURE [PartDesign::Pad] Pad166
  BaseFeature = -> Pocket029
  Direction = (0,0,-1)
  Length = 3.1
  Length2 = 10
  Placement = pos=(0,0,0) rot=(1,0,0;1.5708rad)
  Profile = -> Sketch239
  ReferenceAxis = -> Sketch239 [N_Axis]
  Refine = true
  Suppressed = false
  Type = 0
FEATURE [PartDesign::Fillet] Fillet017
  Base = -> Pad166 [Edge85]
  BaseFeature = -> Pad166
  Placement = pos=(0,0,0) rot=(1,0,0;1.5708rad)
  Radius = 1
  Refine = true
  SupportTransform = false
  Suppressed = false
  UseAllEdges = false
FEATURE [Sketcher::SketchObject] Sketch240
  ArcFitTolerance = 1e-06
  AttachmentSupport = -> [Fillet017]
  ExternalGeometry = -> [Fillet017]
  FullyConstrained = true
  MakeInternals = false
  MapMode = 5
  Placement = pos=(14.2,1.79e-14,0) rot=(0.707107,0,0.707107;3.14159rad)
  sketch-geometry (1):
    g0: Circle CenterX=3 CenterY=1.35 CenterZ=0 NormalX=0 NormalY=0 NormalZ=1 AngleXU=0 Radius=1.6
  constraints (4):
    c: Diameter(g0) = 3.2
    c: DistanceY(g-3,g-3) = 4
    c: DistanceY(g0,g-4) = 2
    c: DistanceX(g-4,g0) = 4
FEATURE [PartDesign::Pad] Pad167
  BaseFeature = -> Fillet017
  Direction = (1,1.3e-15,-2e-16)
  Length = 2
  Length2 = 10
  Placement = pos=(0,0,0) rot=(1,0,0;1.5708rad)
  Profile = -> Sketch240
  ReferenceAxis = -> Sketch240 [N_Axis]
  Refine = true
  Suppressed = false
  Type = 0
FEATURE [Sketcher::SketchObject] Sketch241
  ArcFitTolerance = 1e-06
  AttachmentSupport = -> [Pad167]
  ExternalGeometry = -> [Pad167]
  FullyConstrained = true
  MakeInternals = false
  MapMode = 5
  Placement = pos=(16.2,2.07e-14,-1.2e-14) rot=(0.707107,0,0.707107;3.14159rad)
  sketch-geometry (1):
    g0: Circle CenterX=3 CenterY=1.35 CenterZ=0 NormalX=0 NormalY=0 NormalZ=1 AngleXU=0 Radius=0.9
  constraints (2):
    c: Coincident(g0,g-3)
    c: Diameter(g0) = 1.8
FEATURE [PartDesign::Pad] Pad168
  BaseFeature = -> Pad167
  Direction = (1,1.3e-15,-2e-16)
  Length = 3.6
  Length2 = 10
  Placement = pos=(0,0,0) rot=(1,0,0;1.5708rad)
  Profile = -> Sketch241
  ReferenceAxis = -> Sketch241 [N_Axis]
  Refine = true
  Suppressed = false
  Type = 0
FEATURE [Sketcher::SketchObject] Sketch242
  ArcFitTolerance = 1e-06
  AttachmentSupport = -> [Pad168]
  ExternalGeometry = -> [Pad168]
  FullyConstrained = true
  MakeInternals = false
  MapMode = 5
  Placement = pos=(19.8,4.51e-14,-2.61e-14) rot=(0.707107,0,0.707107;3.14159rad)
  sketch-geometry (1):
    g0: Circle CenterX=3 CenterY=1.35 CenterZ=0 NormalX=0 NormalY=0 NormalZ=1 AngleXU=0 Radius=1.2
  constraints (2):
    c: Coincident(g0,g-3)
    c: Diameter(g0) = 2.4
FEATURE [Sketcher::SketchObject] Sketch243
  ArcFitTolerance = 1e-06
  AttachmentOffset = pos=(0,0,4) rot=(0,0,1;0rad)
  AttachmentSupport = -> [Pad168]
  ExternalGeometry = -> [Pad168]
  FullyConstrained = true
  MakeInternals = false
  MapMode = 5
  Placement = pos=(23.8,5.43e-14,-3.17e-14) rot=(0.707107,0,0.707107;3.14159rad)
  sketch-geometry (1):
    g0: Circle CenterX=3 CenterY=1.35 CenterZ=0 NormalX=0 NormalY=0 NormalZ=1 AngleXU=0 Radius=1.05
  constraints (3):
    c: Coincident(g0,g-3)
    c: Diameter(g-3) = 1.8
    c: Diameter(g0) = 2.1
FEATURE [PartDesign::AdditiveLoft] AdditiveLoft008
  BaseFeature = -> Pad168
  Closed = false
  Placement = pos=(0,0,0) rot=(1,0,0;1.5708rad)
  Profile = -> Sketch242
  Refine = true
  Ruled = false
  Sections = -> [Sketch243]
  Suppressed = false
FEATURE [PartDesign::Fillet] Fillet018
  Base = -> AdditiveLoft008 [Edge148,Edge143,Edge75,Edge74,Edge71,Edge70,Edge146,Edge152,Edge154]
  BaseFeature = -> AdditiveLoft008
  Placement = pos=(0,0,0) rot=(1,0,0;1.5708rad)
  Radius = 0.2
  Refine = true
  SupportTransform = false
  Suppressed = false
  UseAllEdges = false
FEATURE [Sketcher::SketchObject] Sketch244
  ArcFitTolerance = 1e-06
  AttachmentSupport = -> [Fillet018]
  ExternalGeometry = -> [Fillet018]
  FullyConstrained = true
  MakeInternals = false
  MapMode = 5
  Placement = pos=(-1.2e-15,0.942429,0.115581) rot=(-1,0,0;1.44876rad)
  sketch-geometry (8):
    g0: LineSegment StartX=11.9 StartY=-7.74199 StartZ=0 EndX=11.9 EndY=-2.40228 EndZ=0
    g1: LineSegment StartX=14.2 StartY=-2.40228 StartZ=0 EndX=11.9 EndY=-2.40228 EndZ=0
    g2: LineSegment StartX=14.2 StartY=-2.40228 StartZ=0 EndX=14.2 EndY=-7.74199 EndZ=0
    g3: LineSegment StartX=11.9 StartY=-7.74199 StartZ=0 EndX=14.2 EndY=-7.74199 EndZ=0
    g4: LineSegment StartX=8.4 StartY=-7.74199 StartZ=0 EndX=5.92857 EndY=-2.40228 EndZ=0
    g5: LineSegment StartX=3.5 StartY=-2.40228 StartZ=0 EndX=5.92857 EndY=-2.40228 EndZ=0
    g6: LineSegment StartX=3.5 StartY=-2.40228 StartZ=0 EndX=3.5 EndY=-7.74199 EndZ=0
    g7: LineSegment StartX=8.4 StartY=-7.74199 StartZ=0 EndX=3.5 EndY=-7.74199 EndZ=0
  constraints (20):
    c: Coincident(g0,g-11)
    c: Vertical(g0)
    c: Coincident(g1,g-6)
    c: Coincident(g1,g0)
    c: Horizontal(g1)
    c: Coincident(g2,g1)
    c: Vertical(g2)
    c: Coincident(g3,g0)
    c: Coincident(g3,g2)
    c: Horizontal(g3)
    c: Coincident(g4,g-7)
    c: Coincident(g5,g-10)
    c: Coincident(g5,g4)
    c: Horizontal(g5)
    c: Coincident(g6,g5)
    c: Vertical(g6)
    c: Coincident(g7,g6)
    c: Horizontal(g7)
    c: Coincident(g7,g4)
    c: PointOnObject(g-8,g4)
FEATURE [PartDesign::Pocket] Pocket030
  BaseFeature = -> Fillet018
  Direction = (1.2e-15,-0.992563,-0.121729)
  Length = 0.3
  Length2 = 5
  Placement = pos=(0,0,0) rot=(1,0,0;1.5708rad)
  Profile = -> Sketch244
  ReferenceAxis = -> Sketch244 [N_Axis]
  Refine = true
  Suppressed = false
  Type = 0
FEATURE [Sketcher::SketchObject] Sketch245
  ArcFitTolerance = 1e-06
  AttachmentSupport = -> [Pocket030]
  ExternalGeometry = -> [Pocket030]
  FullyConstrained = true
  MakeInternals = false
  MapMode = 5
  Placement = pos=(4.6e-15,-3.60242,0.441806) rot=(1,0,0;1.44876rad)
  sketch-geometry (8):
    g0: LineSegment StartX=8.4 StartY=7.41332 StartZ=0 EndX=5.92857 EndY=2.07361 EndZ=0
    g1: LineSegment StartX=3.5 StartY=2.07361 StartZ=0 EndX=5.92857 EndY=2.07361 EndZ=0
    g2: LineSegment StartX=3.5 StartY=2.07361 StartZ=0 EndX=3.5 EndY=7.41332 EndZ=0
    g3: LineSegment StartX=8.4 StartY=7.41332 StartZ=0 EndX=3.5 EndY=7.41332 EndZ=0
    g4: LineSegment StartX=11.9 StartY=7.41332 StartZ=0 EndX=11.9 EndY=2.07361 EndZ=0
    g5: LineSegment StartX=14.2 StartY=2.07361 StartZ=0 EndX=11.9 EndY=2.07361 EndZ=0
    g6: LineSegment StartX=11.9 StartY=7.41332 StartZ=0 EndX=14.2 EndY=7.41332 EndZ=0
    g7: LineSegment StartX=14.2 StartY=2.07361 StartZ=0 EndX=14.2 EndY=7.41332 EndZ=0
  constraints (20):
    c: Coincident(g0,g-6)
    c: Coincident(g1,g-7)
    c: Coincident(g1,g0)
    c: Horizontal(g1)
    c: PointOnObject(g-6,g0)
    c: Coincident(g2,g1)
    c: Vertical(g2)
    c: Coincident(g3,g0)
    c: Coincident(g3,g2)
    c: Horizontal(g3)
    c: Vertical(g4)
    c: Coincident(g5,g-5)
    c: Coincident(g5,g4)
    c: PointOnObject(g4,g-4)
    c: Coincident(g6,g4)
    c: Horizontal(g6)
    c: Coincident(g7,g5)
    c: Coincident(g7,g6)
    c: Vertical(g7)
    c: Coincident(g4,g-3)
FEATURE [PartDesign::Pocket] Pocket031
  BaseFeature = -> Pocket030
  Direction = (-1.2e-15,0.992563,-0.121729)
  Length = 0.3
  Length2 = 5
  Placement = pos=(0,0,0) rot=(1,0,0;1.5708rad)
  Profile = -> Sketch245
  ReferenceAxis = -> Sketch245 [N_Axis]
  Refine = true
  Suppressed = false
  Type = 0
FEATURE [PartDesign::Body] Body019  label="Mixmaster_Gun"
  AllowCompound = false
  Group = -> [Sketch225,Pad156,Sketch226,Pad157,Sketch227,Pad158,Sketch228,Pad159,Sketch229,Pad160,Sketch230,Sketch231,AdditiveLoft007,Sketch232,Pad161,Sketch233,Pad162,Sketch234,Pocket028,Sketch235,Pad163,Sketch236,Pad164,Sketch237,Pad165,Sketch238,Pocket029,Sketch239,Pad166,Fillet017,Sketch240,Pad167,Sketch241,Pad168,Sketch242,Sketch243,AdditiveLoft008,Fillet018,Sketch244,Pocket030,Sketch245,Pocket031,+13 more]
  Origin = -> Origin021
  Placement = pos=(-43,-1.65,-18) rot=(0,0,1;0rad)
  Tip = -> Fillet019
COMPONENT P3 — recipe-attached ("Longhaul_Gun", modeled in this document).
Construction recipe (the document's own serialized feature program — sketch geometry with constraints, then the solid features built on it; lengths are millimeters unless a unit is written):

FEATURE [Sketcher::SketchObject] Sketch252
  ArcFitTolerance = 1e-06
  AttachmentSupport = -> [XZ_Plane022]
  FullyConstrained = true
  MakeInternals = false
  MapMode = 5
  Placement = pos=(0,0,0) rot=(1,0,0;1.5708rad)
  sketch-geometry (16):
    g0: LineSegment StartX=0.430594 StartY=0 StartZ=0 EndX=4.99289 EndY=0 EndZ=0
    g1: LineSegment StartX=5.34645 StartY=0.146447 StartZ=0 EndX=6.7 EndY=1.5 EndZ=0
    g2: LineSegment StartX=6.7 StartY=1.5 StartZ=0 EndX=6.7 EndY=4.9 EndZ=0
    g3: LineSegment StartX=6.7 StartY=4.9 StartZ=0 EndX=5.31436 EndY=7.3 EndZ=0
    g4: LineSegment StartX=5.31436 StartY=7.3 StartZ=0 EndX=-8.48564 EndY=7.3 EndZ=0
    g5: ArcOfCircle CenterX=-7.74795 CenterY=6.62486 CenterZ=0 NormalX=0 NormalY=0 NormalZ=1 AngleXU=0 Radius=1 StartAngle=2.40043 EndAngle=3.77418
    g6: LineSegment StartX=-8.55446 StartY=6.03362 StartZ=0 EndX=-7.2 EndY=4.3 EndZ=0
    g7: LineSegment StartX=-7.2 StartY=4.3 StartZ=0 EndX=-7.2 EndY=1.7 EndZ=0
    g8: ArcOfCircle CenterX=-6.7 CenterY=1.7 CenterZ=0 NormalX=0 NormalY=0 NormalZ=1 AngleXU=0 Radius=0.5 StartAngle=3.14159 EndAngle=6.28319
    g9: LineSegment StartX=-6.2 StartY=1.7 StartZ=0 EndX=-6.2 EndY=4 EndZ=0
    g10: LineSegment StartX=-6.2 StartY=4 StartZ=0 EndX=-0.6 EndY=4 EndZ=0
    g11: LineSegment StartX=-0.6 StartY=4 StartZ=0 EndX=-0.0638745 EndY=0.42583 EndZ=0
    g12: ArcOfCircle CenterX=4.99289 CenterY=0.5 CenterZ=0 NormalX=0 NormalY=0 NormalZ=1 AngleXU=0 Radius=0.5 StartAngle=4.71239 EndAngle=5.49779
    g13: GeomPoint [constr] X=5.2 Y=0 Z=0
    g14: ArcOfCircle CenterX=0.430594 CenterY=0.5 CenterZ=0 NormalX=0 NormalY=0 NormalZ=1 AngleXU=0 Radius=0.5 StartAngle=3.29048 EndAngle=4.71239
    g15: GeomPoint [constr] X=0 Y=0 Z=0
  constraints (46):
    c: PointOnObject(g13,g-1)
    c: Coincident(g2,g1)
    c: Vertical(g2)
    c: Coincident(g3,g2)
    c: Coincident(g4,g3)
    c: Horizontal(g4)
    c: Coincident(g5,g4)
    c: Coincident(g6,g5)
    c: Coincident(g7,g6)
    c: Vertical(g7)
    c: Coincident(g8,g7)
    c: Coincident(g9,g8)
    c: Coincident(g10,g9)
    c: Horizontal(g10)
    c: Coincident(g11,g10)
    c: DistanceX(g15,g13) = 5.2
    c: Diameter(g8) = 1
    c: Vertical(g9)
    c: Diameter(g5) = 2
    c: DistanceX(g4,g3) = 13.8
    c: DistanceY(g7,g6) = 2.6
    c: Angle(g3,g2) = 2.61799
    c: DistanceY(g2,g3) = 2.4
    c: DistanceY(g2,g2) = 3.4
    c: DistanceY(g15,g3) = 7.3
    c: DistanceX(g10,g10) = 5.6
    c: DistanceY(g15,g10) = 4
    c: DistanceX(g6,g2) = 13.9
    c: DistanceY(g6,g4) = 3
    c: DistanceY(g8,g7) = 0
    c: DistanceY(g8,g8) = 0
    c: Angle(g6,g7) = 2.47837
    c: DistanceY(g8,g4) = 5.6
    c: PointOnObject(g13,g0)
    c: PointOnObject(g13,g1)
    c: Tangent(g0,g12) = -1.5708
    c: Tangent(g1,g12) = -1.5708
    c: PointOnObject(g15,g0)
    c: PointOnObject(g15,g11)
    c: Tangent(g0,g14) = -1.5708
    c: Tangent(g11,g14) = -1.5708
    c: Coincident(g15,g-1)
    c: Radius(g14) = 0.5
    c: Radius(g12) = 0.5
    c: Angle(g1,g0) = 2.35619
    c: Distance(g6) = 2.2
FEATURE [PartDesign::Pad] Pad169
  Direction = (0,-1,2e-16)
  Length = 3
  Length2 = 10
  Placement = pos=(0,0,0) rot=(1,0,0;1.5708rad)
  Profile = -> Sketch252
  ReferenceAxis = -> Sketch252 [N_Axis]
  Refine = true
  Suppressed = false
  Type = 0
FEATURE [PartDesign::Fillet] Fillet020
  Base = -> Pad169 [Edge17]
  BaseFeature = -> Pad169
  Placement = pos=(0,0,0) rot=(1,0,0;1.5708rad)
  Radius = 1
  Refine = true
  SupportTransform = false
  Suppressed = false
  UseAllEdges = false
FEATURE [Sketcher::SketchObject] Sketch253
  ArcFitTolerance = 1e-06
  AttachmentSupport = -> [Fillet020]
  ExternalGeometry = -> [Fillet020]
  FullyConstrained = true
  MakeInternals = false
  MapMode = 5
  Placement = pos=(0,-3,7e-16) rot=(1,0,0;1.5708rad)
  sketch-geometry (4):
    g0: LineSegment StartX=-7.2 StartY=4.3 StartZ=0 EndX=-8.7 EndY=4.3 EndZ=0
    g1: LineSegment StartX=-8.7 StartY=4.3 StartZ=0 EndX=-8.7 EndY=7.3 EndZ=0
    g2: LineSegment StartX=-8.7 StartY=7.3 StartZ=0 EndX=-4.2 EndY=7.3 EndZ=0
    g3: LineSegment StartX=-7.2 StartY=4.3 StartZ=0 EndX=-4.2 EndY=7.3 EndZ=0
  constraints (11):
    c: Coincident(g0,g-4)
    c: Horizontal(g0)
    c: Coincident(g1,g0)
    c: Vertical(g1)
    c: Coincident(g2,g1)
    c: PointOnObject(g2,g-3)
    c: Horizontal(g2)
    c: Coincident(g3,g0)
    c: Coincident(g3,g2)
    c: Angle(g3,g0) = 2.35619
    c: DistanceX(g2,g2) = 4.5
FEATURE [PartDesign::Pocket] Pocket038
  BaseFeature = -> Fillet020
  Direction = (0,1,-2e-16)
  Length = 0.75
  Length2 = 5
  Placement = pos=(0,0,0) rot=(1,0,0;1.5708rad)
  Profile = -> Sketch253
  ReferenceAxis = -> Sketch253 [N_Axis]
  Refine = true
  Suppressed = false
  Type = 0
FEATURE [Sketcher::SketchObject] Sketch254
  ArcFitTolerance = 1e-06
  AttachmentSupport = -> [Pocket038]
  ExternalGeometry = -> [Pocket038]
  FullyConstrained = true
  MakeInternals = false
  MapMode = 5
  Placement = pos=(0,0,0) rot=(-1,0,0;1.5708rad)
  sketch-geometry (4):
    g0: LineSegment StartX=-7.2 StartY=-4.3 StartZ=0 EndX=-4.2 EndY=-7.3 EndZ=0
    g1: LineSegment StartX=-4.2 StartY=-7.3 StartZ=0 EndX=-8.7 EndY=-7.3 EndZ=0
    g2: LineSegment StartX=-8.7 StartY=-7.3 StartZ=0 EndX=-8.7 EndY=-4.3 EndZ=0
    g3: LineSegment StartX=-7.2 StartY=-4.3 StartZ=0 EndX=-8.7 EndY=-4.3 EndZ=0
  constraints (11):
    c: Coincident(g0,g-3)
    c: PointOnObject(g0,g-4)
    c: Coincident(g1,g0)
    c: Horizontal(g1)
    c: Coincident(g2,g1)
    c: Vertical(g2)
    c: Coincident(g3,g0)
    c: Coincident(g3,g2)
    c: Horizontal(g3)
    c: Angle(g3,g0) = 2.35619
    c: DistanceX(g1,g1) = 4.5
FEATURE [PartDesign::Pocket] Pocket039
  BaseFeature = -> Pocket038
  Direction = (0,-1,-2e-16)
  Length = 0.75
  Length2 = 5
  Placement = pos=(0,0,0) rot=(1,0,0;1.5708rad)
  Profile = -> Sketch254
  ReferenceAxis = -> Sketch254 [N_Axis]
  Refine = true
  Suppressed = false
  Type = 0
FEATURE [Sketcher::SketchObject] Sketch255
  ArcFitTolerance = 1e-06
  AttachmentSupport = -> [Pocket039]
  ExternalGeometry = -> [Pocket039]
  FullyConstrained = true
  MakeInternals = false
  MapMode = 5
  Placement = pos=(0,-3,7e-16) rot=(1,0,0;1.5708rad)
  sketch-geometry (8):
    g0: LineSegment StartX=-0.6 StartY=4 StartZ=0 EndX=-0.0638745 EndY=0.42583 EndZ=0
    g1: ArcOfCircle CenterX=0.430594 CenterY=0.5 CenterZ=0 NormalX=0 NormalY=0 NormalZ=1 AngleXU=0 Radius=0.5 StartAngle=3.29048 EndAngle=4.71239
    g2: LineSegment StartX=0.430594 StartY=1e-16 StartZ=0 EndX=4.99289 EndY=9.9e-15 EndZ=0
    g3: ArcOfCircle CenterX=4.99289 CenterY=0.5 CenterZ=0 NormalX=0 NormalY=0 NormalZ=1 AngleXU=0 Radius=0.5 StartAngle=4.71239 EndAngle=5.49779
    g4: LineSegment StartX=5.34645 StartY=0.146447 StartZ=0 EndX=6.7 EndY=1.5 EndZ=0
    g5: LineSegment StartX=6.7 StartY=1.5 StartZ=0 EndX=6.7 EndY=4.9 EndZ=0
    g6: LineSegment StartX=6.7 StartY=4.9 StartZ=0 EndX=0.3 EndY=4.9 EndZ=0
    g7: LineSegment StartX=-0.6 StartY=4 StartZ=0 EndX=0.3 EndY=4.9 EndZ=0
  constraints (18):
    c: Coincident(g0,g-8)
    c: Coincident(g0,g-8)
    c: Coincident(g1,g0)
    c: Tangent(g1,g-7) = -1.5708
    c: Coincident(g2,g1)
    c: Coincident(g2,g-6)
    c: Coincident(g3,g2)
    c: Coincident(g3,g-4)
    c: Tangent(g3,g-3)
    c: Coincident(g4,g-5)
    c: Coincident(g4,g3)
    c: Coincident(g5,g4)
    c: Coincident(g5,g-5)
    c: Coincident(g6,g5)
    c: Horizontal(g6)
    c: Coincident(g7,g0)
    c: Coincident(g7,g6)
    c: Angle(g7,g6) = 2.35619
FEATURE [PartDesign::Pad] Pad170
  BaseFeature = -> Pocket039
  Direction = (0,-1,2e-16)
  Length = 1
  Length2 = 10
  Placement = pos=(0,0,0) rot=(1,0,0;1.5708rad)
  Profile = -> Sketch255
  ReferenceAxis = -> Sketch255 [N_Axis]
  Refine = true
  Suppressed = false
  Type = 0
FEATURE [Sketcher::SketchObject] Sketch256
  ArcFitTolerance = 1e-06
  AttachmentSupport = -> [Pad170]
  ExternalGeometry = -> [Pad170]
  FullyConstrained = true
  MakeInternals = false
  MapMode = 5
  Placement = pos=(0,0,0) rot=(-1,0,0;1.5708rad)
  sketch-geometry (8):
    g0: LineSegment StartX=6.7 StartY=-4.9 StartZ=0 EndX=6.7 EndY=-1.5 EndZ=0
    g1: LineSegment StartX=6.7 StartY=-1.5 StartZ=0 EndX=5.34645 EndY=-0.146447 EndZ=0
    g2: ArcOfCircle CenterX=4.99289 CenterY=-0.5 CenterZ=0 NormalX=0 NormalY=0 NormalZ=1 AngleXU=0 Radius=0.5 StartAngle=0.785398 EndAngle=1.5708
    g3: LineSegment StartX=4.99289 StartY=-2.67e-14 StartZ=0 EndX=0.430594 EndY=-2.66e-14 EndZ=0
    g4: ArcOfCircle CenterX=0.430594 CenterY=-0.5 CenterZ=0 NormalX=0 NormalY=0 NormalZ=1 AngleXU=0 Radius=0.5 StartAngle=1.5708 EndAngle=2.9927
    g5: LineSegment StartX=-0.0638745 StartY=-0.42583 StartZ=0 EndX=-0.6 EndY=-4 EndZ=0
    g6: LineSegment StartX=6.7 StartY=-4.9 StartZ=0 EndX=0.3 EndY=-4.9 EndZ=0
    g7: LineSegment StartX=-0.6 StartY=-4 StartZ=0 EndX=0.3 EndY=-4.9 EndZ=0
  constraints (17):
    c: Coincident(g0,g-8)
    c: Coincident(g0,g-8)
    c: Coincident(g1,g0)
    c: Coincident(g1,g-7)
    c: Coincident(g2,g1)
    c: Tangent(g2,g-6) = -1.5708
    c: Coincident(g3,g2)
    c: Coincident(g3,g-5)
    c: Coincident(g4,g3)
    c: Tangent(g4,g-4) = -1.5708
    c: Coincident(g5,g4)
    c: Coincident(g5,g-3)
    c: Coincident(g6,g0)
    c: Horizontal(g6)
    c: Coincident(g7,g5)
    c: Coincident(g7,g6)
    c: Angle(g6,g7) = 2.35619
FEATURE [PartDesign::Pad] Pad171
  BaseFeature = -> Pad170
  Direction = (0,1,2e-16)
  Length = 1
  Length2 = 10
  Placement = pos=(0,0,0) rot=(1,0,0;1.5708rad)
  Profile = -> Sketch256
  ReferenceAxis = -> Sketch256 [N_Axis]
  Refine = true
  Suppressed = false
  Type = 0
FEATURE [Sketcher::SketchObject] Sketch257
  ArcFitTolerance = 1e-06
  AttachmentSupport = -> [Pad171]
  ExternalGeometry = -> [Pad171]
  FullyConstrained = true
  MakeInternals = false
  MapMode = 5
  Placement = pos=(0,-4,0) rot=(1,0,0;1.5708rad)
  sketch-geometry (3):
    g0: LineSegment StartX=4.49289 StartY=2 StartZ=0 EndX=4.49289 EndY=1.5 EndZ=0
    g1: LineSegment StartX=4.49289 StartY=1.5 StartZ=0 EndX=3.49289 EndY=1.75 EndZ=0
    g2: LineSegment StartX=4.49289 StartY=2 StartZ=0 EndX=3.49289 EndY=1.75 EndZ=0
  constraints (9):
    c: Vertical(g0)
    c: Coincident(g1,g0)
    c: Coincident(g2,g0)
    c: Coincident(g2,g1)
    c: DistanceY(g0,g0) = 0.5
    c: DistanceX(g1,g0) = 1
    c: DistanceY(g1,g0) = 0.25
    c: DistanceY(g-3,g0) = 1.5
    c: DistanceX(g0,g-3) = 0.5
FEATURE [PartDesign::Pocket] Pocket040
  BaseFeature = -> Pad171
  Direction = (0,1,-2e-16)
  Length = 0.3
  Length2 = 5
  Placement = pos=(0,0,0) rot=(1,0,0;1.5708rad)
  Profile = -> Sketch257
  ReferenceAxis = -> Sketch257 [N_Axis]
  Refine = true
  Suppressed = false
  Type = 0
FEATURE [PartDesign::Chamfer] Chamfer
  Angle = 45
  Base = -> Pocket040 [Edge62,Edge60,Edge61]
  BaseFeature = -> Pocket040
  ChamferType = 0
  FlipDirection = false
  Placement = pos=(0,0,0) rot=(1,0,0;1.5708rad)
  Refine = true
  Size = 0.2
  Size2 = 1
  SupportTransform = false
  Suppressed = false
  UseAllEdges = false
FEATURE [Sketcher::SketchObject] Sketch258
  ArcFitTolerance = 1e-06
  AttachmentSupport = -> [Chamfer]
  ExternalGeometry = -> [Chamfer]
  FullyConstrained = true
  MakeInternals = false
  MapMode = 5
  Placement = pos=(0,1,2e-16) rot=(-1,0,0;1.5708rad)
  sketch-geometry (3):
    g0: LineSegment StartX=4.49289 StartY=-2 StartZ=0 EndX=4.49289 EndY=-1.5 EndZ=0
    g1: LineSegment StartX=4.49289 StartY=-1.5 StartZ=0 EndX=3.49289 EndY=-1.75 EndZ=0
    g2: LineSegment StartX=4.49289 StartY=-2 StartZ=0 EndX=3.49289 EndY=-1.75 EndZ=0
  constraints (9):
    c: Vertical(g0)
    c: Coincident(g1,g0)
    c: Coincident(g2,g0)
    c: Coincident(g2,g1)
    c: DistanceY(g0,g0) = 0.5
    c: DistanceY(g0,g1) = 0.25
    c: DistanceX(g1,g0) = 1
    c: DistanceX(g0,g-3) = 0.5
    c: DistanceY(g0,g-3) = 1.5
FEATURE [PartDesign::Pocket] Pocket041
  BaseFeature = -> Chamfer
  Direction = (0,-1,-2e-16)
  Length = 0.3
  Length2 = 5
  Placement = pos=(0,0,0) rot=(1,0,0;1.5708rad)
  Profile = -> Sketch258
  ReferenceAxis = -> Sketch258 [N_Axis]
  Refine = true
  Suppressed = false
  Type = 0
FEATURE [PartDesign::Chamfer] Chamfer001
  Angle = 45
  Base = -> Pocket041 [Edge56,Edge55,Edge54]
  BaseFeature = -> Pocket041
  ChamferType = 0
  FlipDirection = false
  Placement = pos=(0,0,0) rot=(1,0,0;1.5708rad)
  Refine = true
  Size = 0.2
  Size2 = 1
  SupportTransform = false
  Suppressed = false
  UseAllEdges = false
FEATURE [Sketcher::SketchObject] Sketch259
  ArcFitTolerance = 1e-06
  AttachmentSupport = -> [Chamfer001]
  ExternalGeometry = -> [Chamfer001]
  FullyConstrained = true
  MakeInternals = false
  MapMode = 5
  Placement = pos=(-6.2,0,0) rot=(0.707107,0,0.707107;3.14159rad)
  sketch-geometry (4):
    g0: LineSegment StartX=4 StartY=0.4 StartZ=0 EndX=3.2 EndY=0.4 EndZ=0
    g1: LineSegment StartX=4 StartY=0.4 StartZ=0 EndX=4 EndY=2.6 EndZ=0
    g2: LineSegment StartX=4 StartY=2.6 StartZ=0 EndX=3.2 EndY=2.6 EndZ=0
    g3: ArcOfCircle CenterX=3.2 CenterY=1.5 CenterZ=0 NormalX=0 NormalY=0 NormalZ=1 AngleXU=0 Radius=1.1 StartAngle=1.5708 EndAngle=4.71239
  constraints (14):
    c: PointOnObject(g0,g-3)
    c: PointOnObject(g1,g-3)
    c: Coincident(g2,g1)
    c: Horizontal(g2)
    c: Coincident(g3,g2)
    c: Coincident(g3,g0)
    c: Horizontal(g0)
    c: Coincident(g0,g1)
    c: DistanceY(g1,g-3) = 0.4
    c: DistanceY(g-3,g0) = 0.4
    c: DistanceX(g3,g2) = 0
    c: DistanceX(g0,g3) = 0
    c: Radius(g3) = 1.1
    c: DistanceX(g2,g2) = 0.8
FEATURE [PartDesign::Pad] Pad172
  BaseFeature = -> Chamfer001
  Direction = (1,0,-2e-16)
  Length = 1
  Length2 = 10
  Placement = pos=(0,0,0) rot=(1,0,0;1.5708rad)
  Profile = -> Sketch259
  ReferenceAxis = -> Sketch259 [N_Axis]
  Refine = true
  Suppressed = false
  Type = 0
FEATURE [PartDesign::Fillet] Fillet021
  Base = -> Pad172 [Edge97,Edge98,Edge96]
  BaseFeature = -> Pad172
  Placement = pos=(0,0,0) rot=(1,0,0;1.5708rad)
  Radius = 0.25
  Refine = true
  SupportTransform = false
  Suppressed = false
  UseAllEdges = false
FEATURE [Sketcher::SketchObject] Sketch260
  ArcFitTolerance = 1e-06
  AttachmentSupport = -> [Fillet021]
  ExternalGeometry = -> [Fillet021]
  FullyConstrained = true
  MakeInternals = false
  MapMode = 5
  Placement = pos=(-5.2,0,0) rot=(0.707107,0,0.707107;3.14159rad)
  sketch-geometry (4):
    g0: LineSegment StartX=4 StartY=2.6 StartZ=0 EndX=4 EndY=0.4 EndZ=0
    g1: LineSegment StartX=4 StartY=2.6 StartZ=0 EndX=2.9 EndY=2.6 EndZ=0
    g2: LineSegment StartX=4 StartY=0.4 StartZ=0 EndX=2.9 EndY=0.4 EndZ=0
    g3: ArcOfCircle CenterX=2.9 CenterY=1.5 CenterZ=0 NormalX=0 NormalY=0 NormalZ=1 AngleXU=0 Radius=1.1 StartAngle=1.5708 EndAngle=4.71239
  constraints (12):
    c: Coincident(g0,g-4)
    c: Coincident(g0,g-5)
    c: PointOnObject(g1,g-4)
    c: Horizontal(g1)
    c: Coincident(g2,g0)
    c: Horizontal(g2)
    c: Coincident(g3,g2)
    c: Coincident(g3,g1)
    c: DistanceX(g1,g1) = 1.1
    c: DistanceX(g2,g2) = 1.1
    c: DistanceX(g3,g1) = 0
    c: DistanceX(g3,g2) = 0
FEATURE [PartDesign::Pad] Pad173
  BaseFeature = -> Fillet021
  Direction = (1,0,-2e-16)
  Length = 1
  Length2 = 10
  Placement = pos=(0,0,0) rot=(1,0,0;1.5708rad)
  Profile = -> Sketch260
  ReferenceAxis = -> Sketch260 [N_Axis]
  Refine = true
  Suppressed = false
  Type = 0
FEATURE [PartDesign::Fillet] Fillet022
  Base = -> Pad173 [Edge22,Edge21,Edge24,Edge26,Edge25,Edge20]
  BaseFeature = -> Pad173
  Placement = pos=(0,0,0) rot=(1,0,0;1.5708rad)
  Radius = 0.249
  Refine = true
  SupportTransform = false
  Suppressed = false
  UseAllEdges = false
FEATURE [Sketcher::SketchObject] Sketch261
  ArcFitTolerance = 1e-06
  AttachmentSupport = -> [Fillet022]
  ExternalGeometry = -> [Fillet022]
  FullyConstrained = true
  MakeInternals = false
  MapMode = 5
  Placement = pos=(-4.2,0,1.7e-15) rot=(0.707107,0,0.707107;3.14159rad)
  sketch-geometry (4):
    g0: LineSegment StartX=4 StartY=2.6 StartZ=0 EndX=4 EndY=0.4 EndZ=0
    g1: LineSegment StartX=4 StartY=2.6 StartZ=0 EndX=2.7 EndY=2.6 EndZ=0
    g2: LineSegment StartX=4 StartY=0.4 StartZ=0 EndX=2.7 EndY=0.4 EndZ=0
    g3: ArcOfCircle CenterX=2.7 CenterY=1.5 CenterZ=0 NormalX=0 NormalY=0 NormalZ=1 AngleXU=0 Radius=1.1 StartAngle=1.5708 EndAngle=4.71239
  constraints (11):
    c: Coincident(g0,g-4)
    c: Coincident(g0,g-5)
    c: Coincident(g1,g0)
    c: Horizontal(g1)
    c: Coincident(g2,g0)
    c: Horizontal(g2)
    c: Coincident(g3,g2)
    c: Coincident(g3,g1)
    c: DistanceX(g1,g1) = 1.3
    c: DistanceX(g2,g2) = 1.3
    c: DistanceX(g3,g1) = 0
FEATURE [PartDesign::Pad] Pad174
  BaseFeature = -> Fillet022
  Direction = (1,0,-2e-16)
  Length = 1
  Length2 = 10
  Placement = pos=(0,0,0) rot=(1,0,0;1.5708rad)
  Profile = -> Sketch261
  ReferenceAxis = -> Sketch261 [N_Axis]
  Refine = true
  Suppressed = false
  Type = 0
FEATURE [PartDesign::Fillet] Fillet023
  Base = -> Pad174 [Edge32,Edge33,Edge34,Edge36,Edge38,Edge37]
  BaseFeature = -> Pad174
  Placement = pos=(0,0,0) rot=(1,0,0;1.5708rad)
  Radius = 0.248
  Refine = true
  SupportTransform = false
  Suppressed = false
  UseAllEdges = false
FEATURE [Sketcher::SketchObject] Sketch262
  ArcFitTolerance = 1e-06
  AttachmentSupport = -> [Fillet023]
  ExternalGeometry = -> [Fillet023]
  FullyConstrained = true
  MakeInternals = false
  MapMode = 5
  Placement = pos=(-3.2,0,1.1e-15) rot=(0.707107,0,0.707107;3.14159rad)
  sketch-geometry (4):
    g0: LineSegment StartX=4 StartY=2.6 StartZ=0 EndX=4 EndY=0.4 EndZ=0
    g1: LineSegment StartX=4 StartY=0.4 StartZ=0 EndX=2.5 EndY=0.4 EndZ=0
    g2: LineSegment StartX=4 StartY=2.6 StartZ=0 EndX=2.5 EndY=2.6 EndZ=0
    g3: ArcOfCircle CenterX=2.5 CenterY=1.5 CenterZ=0 NormalX=0 NormalY=0 NormalZ=1 AngleXU=0 Radius=1.1 StartAngle=1.5708 EndAngle=4.71239
  constraints (11):
    c: Coincident(g0,g-4)
    c: Coincident(g0,g-5)
    c: Coincident(g1,g0)
    c: Horizontal(g1)
    c: Coincident(g2,g0)
    c: Horizontal(g2)
    c: Coincident(g3,g2)
    c: Coincident(g3,g1)
    c: DistanceX(g2,g2) = 1.5
    c: DistanceX(g1,g1) = 1.5
    c: DistanceX(g3,g2) = 0
FEATURE [PartDesign::Pad] Pad175
  BaseFeature = -> Fillet023
  Direction = (1,0,-2e-16)
  Length = 1
  Length2 = 10
  Placement = pos=(0,0,0) rot=(1,0,0;1.5708rad)
  Profile = -> Sketch262
  ReferenceAxis = -> Sketch262 [N_Axis]
  Refine = true
  Suppressed = false
  Type = 0
FEATURE [PartDesign::Fillet] Fillet024
  Base = -> Pad175 [Edge40,Edge41,Edge42,Edge44,Edge46,Edge45]
  BaseFeature = -> Pad175
  Placement = pos=(0,0,0) rot=(1,0,0;1.5708rad)
  Radius = 0.247
  Refine = true
  SupportTransform = false
  Suppressed = false
  UseAllEdges = false
FEATURE [Sketcher::SketchObject] Sketch263
  ArcFitTolerance = 1e-06
  AttachmentSupport = -> [Fillet024]
  ExternalGeometry = -> [Fillet024]
  FullyConstrained = true
  MakeInternals = false
  MapMode = 5
  Placement = pos=(-2.2,0,0) rot=(0.707107,0,0.707107;3.14159rad)
  sketch-geometry (4):
    g0: LineSegment StartX=4 StartY=2.6 StartZ=0 EndX=4 EndY=0.4 EndZ=0
    g1: LineSegment StartX=4 StartY=2.6 StartZ=0 EndX=2.3 EndY=2.6 EndZ=0
    g2: LineSegment StartX=4 StartY=0.4 StartZ=0 EndX=2.3 EndY=0.4 EndZ=0
    g3: ArcOfCircle CenterX=2.3 CenterY=1.5 CenterZ=0 NormalX=0 NormalY=0 NormalZ=1 AngleXU=0 Radius=1.1 StartAngle=1.5708 EndAngle=4.71239
  constraints (11):
    c: Coincident(g0,g-5)
    c: Coincident(g0,g-4)
    c: Coincident(g1,g0)
    c: Horizontal(g1)
    c: Coincident(g2,g0)
    c: Horizontal(g2)
    c: Coincident(g3,g2)
    c: Coincident(g3,g1)
    c: DistanceX(g1,g1) = 1.7
    c: DistanceX(g2,g2) = 1.7
    c: DistanceX(g3,g2) = 0
FEATURE [PartDesign::Pad] Pad176
  BaseFeature = -> Fillet024
  Direction = (1,0,-2e-16)
  Length = 1
  Length2 = 10
  Placement = pos=(0,0,0) rot=(1,0,0;1.5708rad)
  Profile = -> Sketch263
  ReferenceAxis = -> Sketch263 [N_Axis]
  Refine = true
  Suppressed = false
  Type = 0
FEATURE [PartDesign::Fillet] Fillet025
  Base = -> Pad176 [Edge48,Edge49,Edge50,Edge52,Edge54,Edge53]
  BaseFeature = -> Pad176
  Placement = pos=(0,0,0) rot=(1,0,0;1.5708rad)
  Radius = 0.246
  Refine = true
  SupportTransform = false
  Suppressed = false
  UseAllEdges = false
FEATURE [Sketcher::SketchObject] Sketch264
  ArcFitTolerance = 1e-06
  AttachmentSupport = -> [Fillet025]
  ExternalGeometry = -> [Fillet025]
  FullyConstrained = true
  MakeInternals = false
  MapMode = 5
  Placement = pos=(-1.2,0,0) rot=(0.707107,0,0.707107;3.14159rad)
  sketch-geometry (4):
    g0: LineSegment StartX=4 StartY=2.6 StartZ=0 EndX=4 EndY=0.4 EndZ=0
    g1: LineSegment StartX=4 StartY=0.4 StartZ=0 EndX=2.1 EndY=0.4 EndZ=0
    g2: LineSegment StartX=4 StartY=2.6 StartZ=0 EndX=2.1 EndY=2.6 EndZ=0
    g3: ArcOfCircle CenterX=2.1 CenterY=1.5 CenterZ=0 NormalX=0 NormalY=0 NormalZ=1 AngleXU=0 Radius=1.1 StartAngle=1.5708 EndAngle=4.71239
  constraints (11):
    c: Coincident(g0,g-5)
    c: Coincident(g0,g-4)
    c: Coincident(g1,g0)
    c: Horizontal(g1)
    c: Coincident(g2,g0)
    c: Horizontal(g2)
    c: Coincident(g3,g2)
    c: Coincident(g3,g1)
    c: DistanceX(g2,g2) = 1.9
    c: DistanceX(g1,g1) = 1.9
    c: DistanceX(g3,g2) = 0
FEATURE [PartDesign::Pad] Pad177
  BaseFeature = -> Fillet025
  Direction = (1,0,-2e-16)
  Length = 1.1
  Length2 = 10
  Placement = pos=(0,0,0) rot=(1,0,0;1.5708rad)
  Profile = -> Sketch264
  ReferenceAxis = -> Sketch264 [N_Axis]
  Refine = true
  Suppressed = false
  Type = 0
FEATURE [PartDesign::Fillet] Fillet026
  Base = -> Pad177 [Edge35,Edge34,Edge36]
  BaseFeature = -> Pad177
  Placement = pos=(0,0,0) rot=(1,0,0;1.5708rad)
  Radius = 0.245
  Refine = true
  SupportTransform = false
  Suppressed = false
  UseAllEdges = false
FEATURE [Sketcher::SketchObject] Sketch265
  ArcFitTolerance = 1e-06
  AttachmentSupport = -> [Fillet026]
  ExternalGeometry = -> [Fillet026]
  FullyConstrained = true
  MakeInternals = false
  MapMode = 5
  Placement = pos=(-2.38478,-8e-16,-1.8632) rot=(0.898794,0,-0.438371;3.14159rad)
  sketch-geometry (1):
    g0: Circle CenterX=-9.07796 CenterY=1.5 CenterZ=0 NormalX=0 NormalY=0 NormalZ=1 AngleXU=0 Radius=0.5
  constraints (4):
    c: DistanceX(g-3,g0) = 0.5
    c: Diameter(g0) = 1
    c: DistanceY(g-4,g-3) = 1.5
    c: DistanceY(g0,g-3) = 0.75
FEATURE [PartDesign::Pad] Pad178
  BaseFeature = -> Fillet026
  Direction = (-0.788011,0,-0.615661)
  Length = 0.5
  Length2 = 10
  Placement = pos=(0,0,0) rot=(1,0,0;1.5708rad)
  Profile = -> Sketch265
  ReferenceAxis = -> Sketch265 [N_Axis]
  Refine = true
  Suppressed = false
  Type = 0
FEATURE [PartDesign::Fillet] Fillet027
  Base = -> Pad178 [Edge246]
  BaseFeature = -> Pad178
  Placement = pos=(0,0,0) rot=(1,0,0;1.5708rad)
  Radius = 0.49
  Refine = true
  SupportTransform = false
  Suppressed = false
  UseAllEdges = false
FEATURE [Sketcher::SketchObject] Sketch266
  ArcFitTolerance = 1e-06
  AttachmentSupport = -> [Fillet027]
  ExternalGeometry = -> [Fillet027]
  FullyConstrained = true
  MakeInternals = false
  MapMode = 5
  Placement = pos=(0,0,1.45e-14) rot=(1,0,0;3.14159rad)
  sketch-geometry (1):
    g0: Circle CenterX=2.63613 CenterY=1.5 CenterZ=0 NormalX=0 NormalY=0 NormalZ=1 AngleXU=0 Radius=1.95
  constraints (5):
    c: Diameter(g0) = 3.9
    c: DistanceY(g-4,g-4) = 5
    c: DistanceX(g-7,g-6) = 5.41032
    c: DistanceY(g0,g-7) = 2.5
    c: DistanceX(g-7,g0) = 2.7
FEATURE [PartDesign::Pad] Pad179
  BaseFeature = -> Fillet027
  Direction = (0,3.4e-15,-1)
  Length = 2
  Length2 = 10
  Placement = pos=(0,0,0) rot=(1,0,0;1.5708rad)
  Profile = -> Sketch266
  ReferenceAxis = -> Sketch266 [N_Axis]
  Refine = true
  Suppressed = false
  Type = 0
FEATURE [Sketcher::SketchObject] Sketch267
  ArcFitTolerance = 1e-06
  AttachmentSupport = -> [Pad179]
  ExternalGeometry = -> [Pad179]
  FullyConstrained = true
  MakeInternals = false
  MapMode = 5
  Placement = pos=(0,6.8e-15,-2) rot=(1,0,0;3.14159rad)
  sketch-geometry (1):
    g0: Circle CenterX=2.63613 CenterY=1.5 CenterZ=0 NormalX=0 NormalY=0 NormalZ=1 AngleXU=0 Radius=1.4
  constraints (2):
    c: Coincident(g0,g-3)
    c: Radius(g0) = 1.4
FEATURE [PartDesign::Pad] Pad180
  BaseFeature = -> Pad179
  Direction = (0,3.4e-15,-1)
  Length = 3.2
  Length2 = 10
  Placement = pos=(0,0,0) rot=(1,0,0;1.5708rad)
  Profile = -> Sketch267
  ReferenceAxis = -> Sketch267 [N_Axis]
  Refine = true
  Suppressed = false
  Type = 0
FEATURE [PartDesign::Fillet] Fillet028
  Base = -> Pad180 [Edge245]
  BaseFeature = -> Pad180
  Placement = pos=(0,0,0) rot=(1,0,0;1.5708rad)
  Radius = 0.5
  Refine = true
  SupportTransform = false
  Suppressed = false
  UseAllEdges = false
FEATURE [PartDesign::Body] Body020  label="Longhaul_Gun"
  AllowCompound = false
  Group = -> [Sketch252,Pad169,Fillet020,Sketch253,Pocket038,Sketch254,Pocket039,Sketch255,Pad170,Sketch256,Pad171,Sketch257,Pocket040,Chamfer,Sketch258,Pocket041,Chamfer001,Sketch259,Pad172,Fillet021,Sketch260,Pad173,Fillet022,Sketch261,Pad174,Fillet023,Sketch262,Pad175,Fillet024,Sketch263,Pad176,Fillet025,Sketch264,Pad177,Fillet026,Sketch265,Pad178,Fillet027,Sketch266,Pad179,Sketch267,Pad180,Fillet028,+31 more]
  Origin = -> Origin022
  Placement = pos=(-42.64,-1.5,0) rot=(0,0,1;0rad)
  Tip = -> Pocket045
